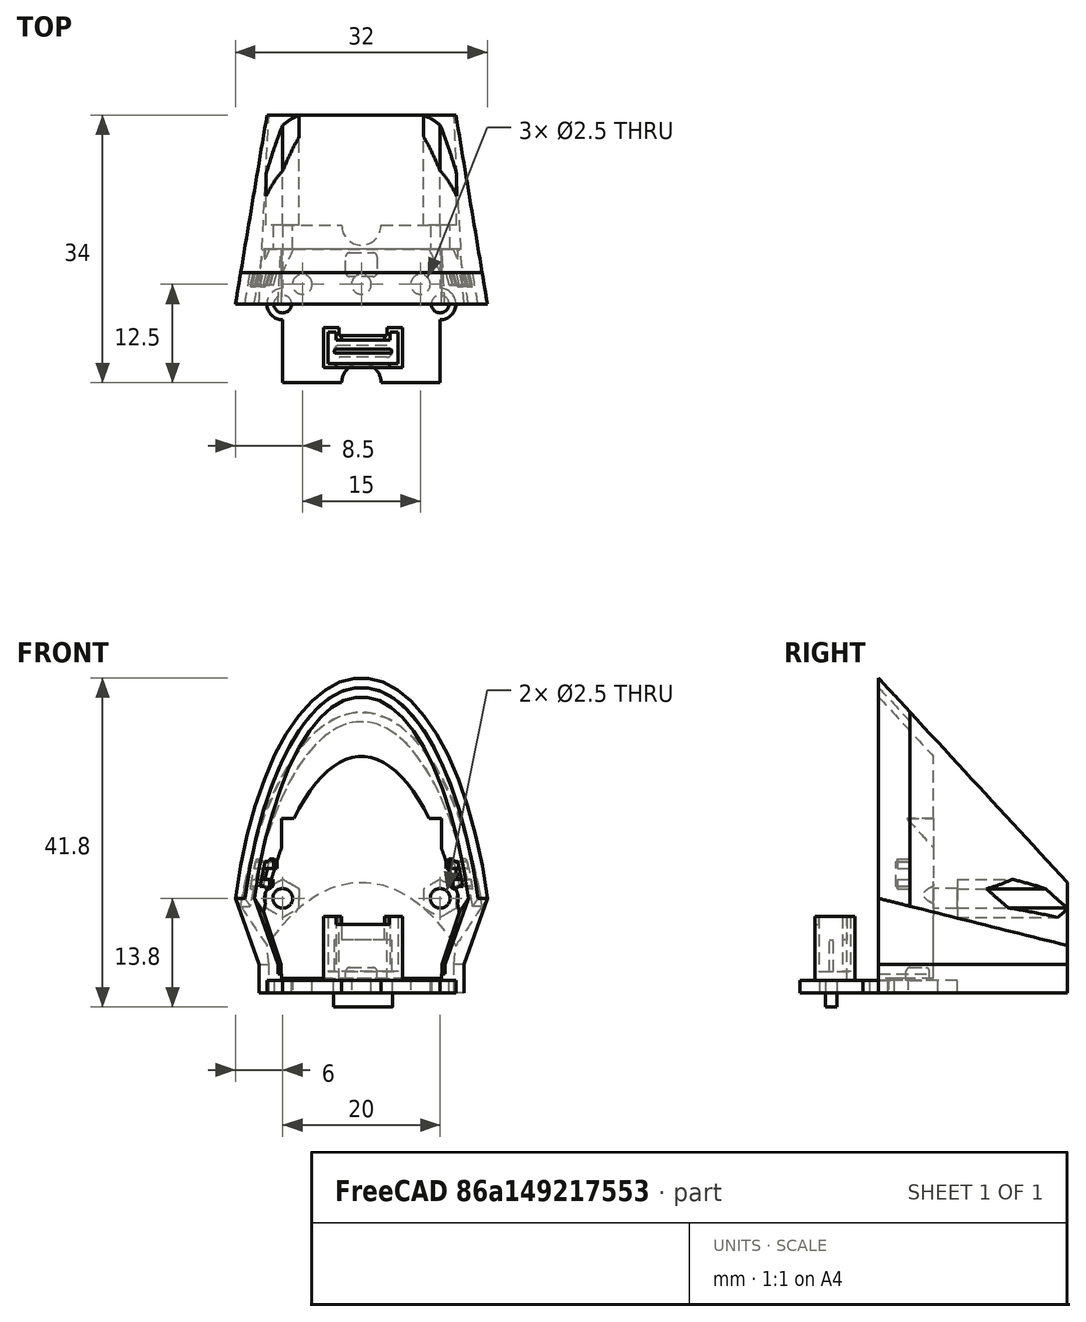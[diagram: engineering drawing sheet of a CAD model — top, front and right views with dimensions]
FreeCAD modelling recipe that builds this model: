
FCSTD DOCUMENT  (FreeCAD 0.19R24276 (Git))
Label: Phoebe_Ear
License: All rights reserved
LicenseURL: http://en.wikipedia.org/wiki/All_rights_reserved
objects: Sketcher::SketchObject×30, PartDesign::Pocket×9, PartDesign::Pad×7, PartDesign::Plane×5, PartDesign::Body×5, PartDesign::SubtractiveLoft×4, PartDesign::AdditiveLoft×2, App::Part×2, Mesh::Feature×2, Spreadsheet::Sheet×1, PartDesign::Fillet×1
note: 86 computed .brp shape members not serialized (recipe doc carries the construction recipe); baked Part::Feature solids carry a one-line shape summary decoded from their .brp

FEATURE [PartDesign::Plane] DatumPlane  label="Datum_EarBack"
  AttachmentOffset = pos=(0,0,-24) rot=(0,0,1;0rad)
  Length = 61.2949
  MapMode = 5
  Placement = pos=(0,24,5.3e-15) rot=(1,0,0;1.5708rad)
  ResizeMode = 0
  Support = -> [XZ_Plane001]
  Width = 75.0828
  expr: .AttachmentOffset.Base.z = -<<params>>.ear_leng
FEATURE [Spreadsheet::Sheet] Spreadsheet  label="params"
  cells = A1=M2 Bolt Clearances; C1=M2.5 Bolt Clearances; E1=Std Dims; G1=Grove Board Dims; A2=Hole Clear Diam; B2(m2_hole_clear_diam)==2.5mm; C2=Hole Clear Diam; D2(m25_hole_clear_diam)==2.8mm; E2=Std. Chamfer; F2(std_chamf)==1mm; G2=Grove Board Width; H2(grove_board_width)==20mm; A3=Head Clear Diam; B3(m2_head_clear_diam)==4.2mm; C3=Head Clear Diam; D3(m25_head_clear_diam)==5.3mm; E3=Std. Radius; F3(std_rad)==2mm; G3=Grove Board Outer Mt Diam; H3(grove_board_mt_outer_diam)==4mm; A4=Head Min Depth; B4(m2_head_min_depth)==1.6mm; C4=Head Min Depth; D4(m25_head_min_depth)==2.3mm; E4=Std. Clear Tol; F4(std_clear_tol)==0.3mm; A5=Nut Clear Flat; B5(m2_nut_clear_flat)==4.2mm; C5=Nut Clear Flat; D5(m25_nut_clear_flat)==5.2mm; A6=Nut Min Depth; B6(m2_nut_min_depth)==1.75mm; C6=Nut Min Depth; D6(m25_nut_min_depth)==2mm; A8=Ear Dims; A9=Ear Base Thick; B9(ear_base_thick)==2mm; C9=Ear Leng; D9(ear_leng)==24mm; E9=Mic Mt Plane Offset Z; F9(mic_mt_plane_offset_z)==7mm; A10=Ear Vert Height; B10(ear_vert_height)==1.6mm; C10=Ear Ellipse Maj Ax; D10(ear_ellipse_majax)==40mm; E10=Mic Mt Hex Offset; F10(mic_mt_hex_offset)==3mm; A12=Ear Fr Base Width; B12(ear_front_base_width)==26mm; C12=Ear Mt Hole Offset; D12(ear_mt_hole_offset)==2.5mm; A13=Ear Fr Mid Width; B13(ear_front_mid_width)==32mm; C13=Ear Mt Hole Width Space; D13(ear_mt_hole_width)==15mm; A14=Ear Fr Mid Height; B14(ear_front_mid_height)==12mm; A15=Ear Fr Tot Height; B15(ear_front_tot_height)==40mm; C15=Ear Wall Thick; D15(ear_wall_thick)==2.4mm; G15=Ear Trm Leng; H15(ear_trim_leng)==4mm; G16=Ear Trm Thick; H16(ear_trim_thick)==1.2mm; A17=Ear Bk Base Width; B17(ear_back_base_width)==23.5mm; C17=Ear Sl Base Width; D17(ear_slope_base_width)==(ear_front_base_width - ear_back_base_width) / ear_leng; E17=Ear GM Base Width; F17(ear_gm_base_width)==ear_front_base_width - ear_slope_base_width * mic_mt_plane_offset_z; G17=Ear Trm Base Width; H17(ear_trim_base_width)==ear_front_base_width - ear_slope_base_width * ear_trim_leng; A18=Ear Bk Mid Width; B18(ear_back_mid_width)==24mm; C18=Ear Sl Mid Width; D18(ear_slope_mid_width)==(ear_front_mid_width - ear_back_mid_width) / ear_leng; E18=Ear GM Mid Width; F18(ear_gm_mid_width)==ear_front_mid_width - ear_slope_mid_width * mic_mt_plane_offset_z; G18=Ear Trm Mid Width; H18(ear_trim_mid_width)==ear_front_mid_width - ear_slope_mid_width * ear_trim_leng; A19=Ear Bk Mid Height; B19(ear_back_mid_height)==6mm; C19=Ear Sl Mid Height; D19(ear_slope_mid_height)==(ear_front_mid_height - ear_back_mid_height) / ear_leng; E19=Ear GM Mid Height; F19(ear_gm_mid_height)==ear_front_mid_height - ear_slope_mid_height * mic_mt_plane_offset_z; G19=Ear Trm Mid Height; H19(ear_trim_mid_height)==ear_front_mid_height - ear_slope_mid_height * ear_trim_leng; A20=Ear Bk Tot Height; B20(ear_back_tot_height)==14mm; C20=Ear Sl Tot Height; D20(ear_slope_tot_height)==(ear_front_tot_height - ear_back_tot_height) / ear_leng; E20=Ear GM Tot Height; F20(ear_gm_tot_height)==ear_front_tot_height - ear_slope_tot_height * mic_mt_plane_offset_z; G20=Ear Trm Tot Height; H20(ear_trim_tot_height)==ear_front_tot_height - ear_slope_tot_height * ear_trim_leng; G22=Ear Trm Clip Width; H22(ear_trim_clip_width)==1.6mm; G23=Ear Trm Clip Height; H23(ear_trim_clip_height)==3mm; G24=Ear Trm Clip Tol; H24(ear_trim_clip_tol)==0.2mm; G25=Ear Trm Clip Thick; H25(ear_trim_clip_thick)==0.8mm; G26=Ear Trm Clip Wedge Size; H26(ear_trim_clip_wedge_size)==0.4mm; G27=Ear Trm Clip Leng; H27(ear_trim_clip_leng)==ear_wall_thick - ear_trim_thick + ear_trim_clip_tol
FEATURE [Sketcher::SketchObject] Sketch  label="Sketch_EarFront"
  FullyConstrained = true
  MapMode = 5
  Placement = pos=(0,0,0) rot=(1,0,0;1.5708rad)
  Support = -> [XZ_Plane001]
  expr: Constraints[30] = <<params>>.ear_base_thick + <<params>>.ear_vert_height
  expr: Constraints[31] = <<params>>.ear_front_mid_height
  expr: Constraints[32] = <<params>>.ear_front_mid_width
  expr: Constraints[33] = <<params>>.ear_front_base_width
  expr: Constraints[34] = <<params>>.ear_front_tot_height
  expr: Constraints[35] = <<params>>.ear_ellipse_majax
  sketch-geometry (15):
    g0: LineSegment StartX=-13 StartY=0 StartZ=0 EndX=13 EndY=0 EndZ=0
    g1: LineSegment StartX=-13 StartY=0 StartZ=0 EndX=-13 EndY=3.6 EndZ=0
    g2: LineSegment StartX=13 StartY=0 StartZ=0 EndX=13 EndY=3.6 EndZ=0
    g3: LineSegment StartX=-13 StartY=3.6 StartZ=0 EndX=13 EndY=3.6 EndZ=0
    g4: LineSegment StartX=13 StartY=3.6 StartZ=0 EndX=16 EndY=12 EndZ=0
    g5: LineSegment StartX=-13 StartY=3.6 StartZ=0 EndX=-16 EndY=12 EndZ=0
    g6: ArcOfEllipse CenterX=0 CenterY=4e-16 CenterZ=0 NormalX=0 NormalY=0 NormalZ=1 MajorRadius=40 MinorRadius=16.7726 AngleXU=1.5708 StartAngle=5.01708 EndAngle=7.54929
    g7: LineSegment StartX=0 StartY=40 StartZ=0 EndX=0 EndY=-40 EndZ=0
    g8: LineSegment StartX=-16.7726 StartY=4e-16 StartZ=0 EndX=16.7726 EndY=4e-16 EndZ=0
    g9: GeomPoint X=0 Y=36.3137 Z=0
    g10: GeomPoint X=0 Y=-36.3137 Z=0
    g11: LineSegment StartX=-16 StartY=12 StartZ=0 EndX=16 EndY=12 EndZ=0
    g12: LineSegment StartX=-13 StartY=3.6 StartZ=0 EndX=-13 EndY=12 EndZ=0
    g13: LineSegment StartX=13 StartY=3.6 StartZ=0 EndX=13 EndY=12 EndZ=0
    g14: LineSegment StartX=-16 StartY=12 StartZ=0 EndX=16 EndY=12 EndZ=0
  constraints (33):
    c: Horizontal(g0)
    c: Symmetric(g0,g0,g-1)
    c: Coincident(g1,g0)
    c: Vertical(g1)
    c: Coincident(g2,g0)
    c: Vertical(g2)
    c: Coincident(g3,g1)
    c: Coincident(g3,g2)
    c: Horizontal(g3)
    c: Coincident(g4,g2)
    c: Coincident(g5,g1)
    c: InternalAlignment(g7-g10 -> g6) x4
    c: PointOnObject(g6,g-2)
    c: Coincident(g11,g5)
    c: Coincident(g11,g4)
    c: Horizontal(g11)
    c: Coincident(g12,g1)
    c: PointOnObject(g12,g11)
    c: Vertical(g12)
    c: Coincident(g13,g2)
    c: PointOnObject(g13,g11)
    c: Vertical(g13)
    c: PointOnObject(g7,g-2)
    c: Coincident(g14,g6)
    c: Coincident(g14,g6)
    c: Coincident(g6,g5)
    c: Coincident(g6,g4)
    c: DistanceY(g0,g2) = 3.6
    c: DistanceY(g-1,g4) = 12
    c: DistanceX(g5,g4) = 32
    c: DistanceX(g0,g0) = 26
    c: DistanceY(g-1,g7) = 40
    c: DistanceY(g8,g7) = 40
FEATURE [Sketcher::SketchObject] Sketch001  label="Sketch_EarBack"
  FullyConstrained = true
  MapMode = 5
  Placement = pos=(0,24,5.3e-15) rot=(1,0,0;1.5708rad)
  Support = -> [DatumPlane]
  expr: Constraints[33] = <<params>>.ear_back_base_width
  expr: Constraints[32] = <<params>>.ear_back_mid_width
  expr: Constraints[31] = <<params>>.ear_back_mid_height
  expr: Constraints[30] = <<params>>.ear_base_thick + <<params>>.ear_vert_height
  expr: Constraints[34] = <<params>>.ear_back_tot_height
  expr: Constraints[35] = <<params>>.ear_ellipse_majax
  sketch-geometry (15):
    g0: LineSegment StartX=-11.75 StartY=0 StartZ=0 EndX=11.75 EndY=0 EndZ=0
    g1: LineSegment StartX=-11.75 StartY=0 StartZ=0 EndX=-11.75 EndY=3.6 EndZ=0
    g2: LineSegment StartX=11.75 StartY=0 StartZ=0 EndX=11.75 EndY=3.6 EndZ=0
    g3: LineSegment StartX=-11.75 StartY=3.6 StartZ=0 EndX=11.75 EndY=3.6 EndZ=0
    g4: LineSegment StartX=11.75 StartY=3.6 StartZ=0 EndX=12 EndY=6 EndZ=0
    g5: LineSegment StartX=-11.75 StartY=3.6 StartZ=0 EndX=-12 EndY=6 EndZ=0
    g6: ArcOfEllipse CenterX=0 CenterY=-26 CenterZ=0 NormalX=0 NormalY=0 NormalZ=1 MajorRadius=40 MinorRadius=20 AngleXU=1.5708 StartAngle=5.63968 EndAngle=6.92669
    g7: LineSegment StartX=0 StartY=14 StartZ=0 EndX=0 EndY=-66 EndZ=0
    g8: LineSegment StartX=-20 StartY=-26 StartZ=0 EndX=20 EndY=-26 EndZ=0
    g9: GeomPoint X=0 Y=8.64102 Z=0
    g10: GeomPoint X=0 Y=-60.641 Z=0
    g11: LineSegment StartX=-12 StartY=6 StartZ=0 EndX=12 EndY=6 EndZ=0
    g12: LineSegment StartX=-11.75 StartY=3.6 StartZ=0 EndX=-11.75 EndY=6 EndZ=0
    g13: LineSegment StartX=11.75 StartY=3.6 StartZ=0 EndX=11.75 EndY=6 EndZ=0
    g14: LineSegment StartX=-12 StartY=6 StartZ=0 EndX=12 EndY=6 EndZ=0
  constraints (33):
    c: Horizontal(g0)
    c: Symmetric(g0,g0,g-1)
    c: Coincident(g1,g0)
    c: Vertical(g1)
    c: Coincident(g2,g0)
    c: Vertical(g2)
    c: Coincident(g3,g1)
    c: Coincident(g3,g2)
    c: Horizontal(g3)
    c: Coincident(g4,g2)
    c: Coincident(g5,g1)
    c: InternalAlignment(g7-g10 -> g6) x4
    c: PointOnObject(g6,g-2)
    c: Coincident(g11,g5)
    c: Coincident(g11,g4)
    c: Horizontal(g11)
    c: Coincident(g12,g1)
    c: PointOnObject(g12,g11)
    c: Vertical(g12)
    c: Coincident(g13,g2)
    c: PointOnObject(g13,g11)
    c: Vertical(g13)
    c: PointOnObject(g7,g-2)
    c: Coincident(g14,g6)
    c: Coincident(g14,g6)
    c: Coincident(g6,g5)
    c: Coincident(g6,g4)
    c: DistanceY(g0,g2) = 3.6
    c: DistanceY(g-1,g4) = 6
    c: DistanceX(g5,g4) = 24
    c: DistanceX(g0,g0) = 23.5
    c: DistanceY(g-1,g7) = 14
    c: DistanceY(g6,g7) = 40
FEATURE [PartDesign::AdditiveLoft] AdditiveLoft  label="AdditiveLoft_MainEar"
  Closed = false
  Placement = pos=(0,0,0) rot=(1,0,0;1.5708rad)
  Profile = -> Sketch
  Ruled = false
  Sections = -> [Sketch001]
FEATURE [Sketcher::SketchObject] Sketch002
  FullyConstrained = true
  MapMode = 5
  Support = -> [XY_Plane001]
  expr: Constraints[7] = <<params>>.ear_mt_hole_width
  expr: Constraints[8] = <<params>>.ear_mt_hole_offset
  expr: Constraints[9] = <<params>>.m2_hole_clear_diam
  sketch-geometry (5):
    g0: LineSegment StartX=-7.5 StartY=2.5 StartZ=0 EndX=7.5 EndY=2.5 EndZ=0
    g1: GeomPoint X=0 Y=2.5 Z=0
    g2: Circle CenterX=0 CenterY=2.5 CenterZ=0 NormalX=0 NormalY=0 NormalZ=1 AngleXU=0 Radius=1.25
    g3: Circle CenterX=7.5 CenterY=2.5 CenterZ=0 NormalX=0 NormalY=0 NormalZ=1 AngleXU=0 Radius=1.25
    g4: Circle CenterX=-7.5 CenterY=2.5 CenterZ=0 NormalX=0 NormalY=0 NormalZ=1 AngleXU=0 Radius=1.25
  constraints (11):
    c: Horizontal(g0)
    c: PointOnObject(g1,g-2)
    c: Symmetric(g0,g0,g1)
    c: Coincident(g2,g1)
    c: Coincident(g3,g0)
    c: Coincident(g4,g0)
    c: Equal(g2,g3)
    c: DistanceX(g4,g3) = 15
    c: DistanceY(g-1,g2) = 2.5
    c: Diameter(g3) = 2.5
    c: Equal(g2,g4)
FEATURE [PartDesign::Pocket] Pocket  label="Pocket_MtHoles"
  BaseFeature = -> AdditiveLoft
  Length = 6
  Length2 = 100
  Placement = pos=(0,0,0) rot=(1,0,0;1.5708rad)
  Profile = -> Sketch002
  Reversed = true
  Type = 0
  expr: Length = <<params>>.ear_base_thick * 3
FEATURE [Sketcher::SketchObject] Sketch003  label="Sketch_EarFr_Temp"
  FullyConstrained = true
  MapMode = 5
  Placement = pos=(0,0,0) rot=(1,0,0;1.5708rad)
  Support = -> [XZ_Plane001]
  expr: Constraints[35] = <<params>>.ear_ellipse_majax
  expr: Constraints[34] = <<params>>.ear_front_tot_height
  expr: Constraints[33] = <<params>>.ear_front_base_width
  expr: Constraints[32] = <<params>>.ear_front_mid_width
  expr: Constraints[31] = <<params>>.ear_front_mid_height
  expr: Constraints[30] = <<params>>.ear_base_thick + <<params>>.ear_vert_height
  sketch-geometry (15):
    g0: LineSegment StartX=-13 StartY=0 StartZ=0 EndX=13 EndY=0 EndZ=0
    g1: LineSegment StartX=-13 StartY=0 StartZ=0 EndX=-13 EndY=3.6 EndZ=0
    g2: LineSegment StartX=13 StartY=0 StartZ=0 EndX=13 EndY=3.6 EndZ=0
    g3: LineSegment StartX=-13 StartY=3.6 StartZ=0 EndX=13 EndY=3.6 EndZ=0
    g4: LineSegment StartX=13 StartY=3.6 StartZ=0 EndX=16 EndY=12 EndZ=0
    g5: LineSegment StartX=-13 StartY=3.6 StartZ=0 EndX=-16 EndY=12 EndZ=0
    g6: ArcOfEllipse CenterX=0 CenterY=-7e-16 CenterZ=0 NormalX=0 NormalY=0 NormalZ=1 MajorRadius=40 MinorRadius=16.7726 AngleXU=1.5708 StartAngle=5.01708 EndAngle=7.54929
    g7: LineSegment StartX=0 StartY=40 StartZ=0 EndX=0 EndY=-40 EndZ=0
    g8: LineSegment StartX=-16.7726 StartY=-7e-16 StartZ=0 EndX=16.7726 EndY=-7e-16 EndZ=0
    g9: GeomPoint X=0 Y=36.3137 Z=0
    g10: GeomPoint X=0 Y=-36.3137 Z=0
    g11: LineSegment StartX=-16 StartY=12 StartZ=0 EndX=16 EndY=12 EndZ=0
    g12: LineSegment StartX=-13 StartY=3.6 StartZ=0 EndX=-13 EndY=12 EndZ=0
    g13: LineSegment StartX=13 StartY=3.6 StartZ=0 EndX=13 EndY=12 EndZ=0
    g14: LineSegment StartX=-16 StartY=12 StartZ=0 EndX=16 EndY=12 EndZ=0
  constraints (33):
    c: Horizontal(g0)
    c: Symmetric(g0,g0,g-1)
    c: Coincident(g1,g0)
    c: Vertical(g1)
    c: Coincident(g2,g0)
    c: Vertical(g2)
    c: Coincident(g3,g1)
    c: Coincident(g3,g2)
    c: Horizontal(g3)
    c: Coincident(g4,g2)
    c: Coincident(g5,g1)
    c: InternalAlignment(g7-g10 -> g6) x4
    c: PointOnObject(g6,g-2)
    c: Coincident(g11,g5)
    c: Coincident(g11,g4)
    c: Horizontal(g11)
    c: Coincident(g12,g1)
    c: PointOnObject(g12,g11)
    c: Vertical(g12)
    c: Coincident(g13,g2)
    c: PointOnObject(g13,g11)
    c: Vertical(g13)
    c: PointOnObject(g7,g-2)
    c: Coincident(g14,g6)
    c: Coincident(g14,g6)
    c: Coincident(g6,g5)
    c: Coincident(g6,g4)
    c: DistanceY(g0,g2) = 3.6
    c: DistanceY(g-1,g4) = 12
    c: DistanceX(g5,g4) = 32
    c: DistanceX(g0,g0) = 26
    c: DistanceY(g-1,g7) = 40
    c: DistanceY(g8,g7) = 40
FEATURE [Sketcher::SketchObject] Sketch004  label="Sketch_EarBk_Temp"
  FullyConstrained = true
  MapMode = 5
  Placement = pos=(0,24,5.3e-15) rot=(1,0,0;1.5708rad)
  Support = -> [DatumPlane]
  expr: Constraints[35] = <<params>>.ear_ellipse_majax
  expr: Constraints[34] = <<params>>.ear_back_tot_height
  expr: Constraints[30] = <<params>>.ear_base_thick + <<params>>.ear_vert_height
  expr: Constraints[31] = <<params>>.ear_back_mid_height
  expr: Constraints[32] = <<params>>.ear_back_mid_width
  expr: Constraints[33] = <<params>>.ear_back_base_width
  sketch-geometry (15):
    g0: LineSegment StartX=-11.75 StartY=0 StartZ=0 EndX=11.75 EndY=0 EndZ=0
    g1: LineSegment StartX=-11.75 StartY=0 StartZ=0 EndX=-11.75 EndY=3.6 EndZ=0
    g2: LineSegment StartX=11.75 StartY=0 StartZ=0 EndX=11.75 EndY=3.6 EndZ=0
    g3: LineSegment StartX=-11.75 StartY=3.6 StartZ=0 EndX=11.75 EndY=3.6 EndZ=0
    g4: LineSegment StartX=11.75 StartY=3.6 StartZ=0 EndX=12 EndY=6 EndZ=0
    g5: LineSegment StartX=-11.75 StartY=3.6 StartZ=0 EndX=-12 EndY=6 EndZ=0
    g6: ArcOfEllipse CenterX=0 CenterY=-26 CenterZ=0 NormalX=0 NormalY=0 NormalZ=1 MajorRadius=40 MinorRadius=20 AngleXU=1.5708 StartAngle=5.63968 EndAngle=6.92669
    g7: LineSegment StartX=0 StartY=14 StartZ=0 EndX=0 EndY=-66 EndZ=0
    g8: LineSegment StartX=-20 StartY=-26 StartZ=0 EndX=20 EndY=-26 EndZ=0
    g9: GeomPoint X=0 Y=8.64102 Z=0
    g10: GeomPoint X=0 Y=-60.641 Z=0
    g11: LineSegment StartX=-12 StartY=6 StartZ=0 EndX=12 EndY=6 EndZ=0
    g12: LineSegment StartX=-11.75 StartY=3.6 StartZ=0 EndX=-11.75 EndY=6 EndZ=0
    g13: LineSegment StartX=11.75 StartY=3.6 StartZ=0 EndX=11.75 EndY=6 EndZ=0
    g14: LineSegment StartX=-12 StartY=6 StartZ=0 EndX=12 EndY=6 EndZ=0
  constraints (33):
    c: Horizontal(g0)
    c: Symmetric(g0,g0,g-1)
    c: Coincident(g1,g0)
    c: Vertical(g1)
    c: Coincident(g2,g0)
    c: Vertical(g2)
    c: Coincident(g3,g1)
    c: Coincident(g3,g2)
    c: Horizontal(g3)
    c: Coincident(g4,g2)
    c: Coincident(g5,g1)
    c: InternalAlignment(g7-g10 -> g6) x4
    c: PointOnObject(g6,g-2)
    c: Coincident(g11,g5)
    c: Coincident(g11,g4)
    c: Horizontal(g11)
    c: Coincident(g12,g1)
    c: PointOnObject(g12,g11)
    c: Vertical(g12)
    c: Coincident(g13,g2)
    c: PointOnObject(g13,g11)
    c: Vertical(g13)
    c: PointOnObject(g7,g-2)
    c: Coincident(g14,g6)
    c: Coincident(g14,g6)
    c: Coincident(g6,g5)
    c: Coincident(g6,g4)
    c: DistanceY(g0,g2) = 3.6
    c: DistanceY(g-1,g4) = 6
    c: DistanceX(g5,g4) = 24
    c: DistanceX(g0,g0) = 23.5
    c: DistanceY(g-1,g7) = 14
    c: DistanceY(g6,g7) = 40
FEATURE [Sketcher::SketchObject] Sketch005
  FullyConstrained = true
  MapMode = 5
  Support = -> [XY_Plane003]
  sketch-geometry (16):
    g0: LineSegment StartX=-10 StartY=10 StartZ=0 EndX=-2.5 EndY=10 EndZ=0
    g1: LineSegment StartX=2.5 StartY=10 StartZ=0 EndX=10 EndY=10 EndZ=0
    g2: LineSegment StartX=10 StartY=10 StartZ=0 EndX=10 EndY=2 EndZ=0
    g3: LineSegment StartX=10 StartY=-2 StartZ=0 EndX=10 EndY=-10 EndZ=0
    g4: LineSegment StartX=10 StartY=-10 StartZ=0 EndX=2.5 EndY=-10 EndZ=0
    g5: LineSegment StartX=-2.5 StartY=-10 StartZ=0 EndX=-10 EndY=-10 EndZ=0
    g6: LineSegment StartX=-10 StartY=-10 StartZ=0 EndX=-10 EndY=-2 EndZ=0
    g7: LineSegment StartX=-10 StartY=10 StartZ=0 EndX=-10 EndY=2 EndZ=0
    g8: ArcOfCircle CenterX=0 CenterY=10 CenterZ=0 NormalX=0 NormalY=0 NormalZ=1 AngleXU=0 Radius=2.5 StartAngle=3.14159 EndAngle=6.28319
    g9: ArcOfCircle CenterX=0 CenterY=-10 CenterZ=0 NormalX=0 NormalY=0 NormalZ=1 AngleXU=0 Radius=2.5 StartAngle=0 EndAngle=3.14159
    g10: LineSegment StartX=-2.5 StartY=10 StartZ=0 EndX=2.5 EndY=10 EndZ=0
    g11: LineSegment StartX=-2.5 StartY=-10 StartZ=0 EndX=2.5 EndY=-10 EndZ=0
    g12: LineSegment StartX=-10 StartY=2 StartZ=0 EndX=-10 EndY=-2 EndZ=0
    g13: LineSegment StartX=10 StartY=2 StartZ=0 EndX=10 EndY=-2 EndZ=0
    g14: ArcOfCircle CenterX=-10 CenterY=0 CenterZ=0 NormalX=0 NormalY=0 NormalZ=1 AngleXU=0 Radius=2 StartAngle=1.5708 EndAngle=4.71239
    g15: ArcOfCircle CenterX=10 CenterY=0 CenterZ=0 NormalX=0 NormalY=0 NormalZ=1 AngleXU=0 Radius=2 StartAngle=4.71239 EndAngle=7.85398
  constraints (48):
    c: Horizontal(g0)
    c: Horizontal(g1)
    c: Coincident(g2,g1)
    c: Vertical(g2)
    c: Vertical(g3)
    c: Coincident(g4,g3)
    c: Horizontal(g4)
    c: Horizontal(g5)
    c: Coincident(g6,g5)
    c: Vertical(g6)
    c: Coincident(g7,g0)
    c: Vertical(g7)
    c: PointOnObject(g8,g-2)
    c: Coincident(g8,g0)
    c: Coincident(g8,g1)
    c: PointOnObject(g9,g-2)
    c: Coincident(g9,g5)
    c: Coincident(g9,g4)
    c: Coincident(g10,g0)
    c: Coincident(g10,g1)
    c: Coincident(g11,g5)
    c: Coincident(g11,g4)
    c: Horizontal(g11)
    c: PointOnObject(g9,g11)
    c: PointOnObject(g8,g10)
    c: Horizontal(g10)
    c: Coincident(g12,g7)
    c: Coincident(g12,g6)
    c: Coincident(g13,g2)
    c: Coincident(g13,g3)
    c: Equal(g10,g11)
    c: Equal(g13,g12)
    c: Vertical(g12)
    c: Vertical(g13)
    c: PointOnObject(g14,g-1)
    c: Coincident(g14,g7)
    c: Coincident(g14,g6)
    c: PointOnObject(g15,g-1)
    c: Coincident(g15,g2)
    c: Coincident(g15,g3)
    c: PointOnObject(g14,g12)
    c: PointOnObject(g15,g13)
    c: Equal(g7,g6)
    c: Equal(g1,g0)
    c: Diameter(g14) = 4
    c: Diameter(g8) = 5
    c: DistanceY(g3,g1) = 20
    c: DistanceX(g0,g1) = 20
FEATURE [PartDesign::Pad] Pad
  Direction = (1,1,1)
  Length = 1.6
  Length2 = 100
  Profile = -> Sketch005
  Type = 0
FEATURE [Sketcher::SketchObject] Sketch006
  FullyConstrained = true
  MapMode = 5
  Support = -> [XY_Plane003]
  sketch-geometry (2):
    g0: Circle CenterX=-10 CenterY=0 CenterZ=0 NormalX=0 NormalY=0 NormalZ=1 AngleXU=0 Radius=1.125
    g1: Circle CenterX=10 CenterY=0 CenterZ=0 NormalX=0 NormalY=0 NormalZ=1 AngleXU=0 Radius=1.125
  constraints (5):
    c: PointOnObject(g1,g-1)
    c: Symmetric(g0,g1,g-1)
    c: Equal(g0,g1)
    c: Diameter(g0) = 2.25
    c: DistanceX(g0,g1) = 20
FEATURE [PartDesign::Pocket] Pocket006
  BaseFeature = -> Pad
  Length = 5
  Length2 = 100
  Profile = -> Sketch006
  Reversed = true
  Type = 1
FEATURE [PartDesign::Body] Body007  label="GroveBoard"
  Group = -> [Sketch005,Pad,Sketch006,Pocket006]
  Origin = -> Origin002
  Tip = -> Pocket006
FEATURE [Sketcher::SketchObject] Sketch008
  FullyConstrained = true
  MapMode = 5
  Support = -> [XY_Plane007]
  sketch-geometry (8):
    g0: LineSegment StartX=-5 StartY=0 StartZ=0 EndX=-3.05 EndY=0 EndZ=0
    g1: LineSegment StartX=3.05 StartY=0 StartZ=0 EndX=5 EndY=0 EndZ=0
    g2: LineSegment StartX=-5 StartY=0 StartZ=0 EndX=-5 EndY=5.1 EndZ=0
    g3: LineSegment StartX=-5 StartY=5.1 StartZ=0 EndX=5 EndY=5.1 EndZ=0
    g4: LineSegment StartX=5 StartY=5.1 StartZ=0 EndX=5 EndY=0 EndZ=0
    g5: LineSegment StartX=3.05 StartY=0 StartZ=0 EndX=3.05 EndY=1 EndZ=0
    g6: LineSegment StartX=3.05 StartY=1 StartZ=0 EndX=-3.05 EndY=1 EndZ=0
    g7: LineSegment StartX=-3.05 StartY=1 StartZ=0 EndX=-3.05 EndY=0 EndZ=0
  constraints (23):
    c: PointOnObject(g0,g-1)
    c: PointOnObject(g1,g-1)
    c: PointOnObject(g0,g-1)
    c: Coincident(g2,g0)
    c: Vertical(g2)
    c: Coincident(g3,g2)
    c: Horizontal(g3)
    c: Coincident(g4,g3)
    c: Coincident(g4,g1)
    c: Vertical(g4)
    c: Coincident(g5,g1)
    c: Vertical(g5)
    c: Coincident(g6,g5)
    c: Horizontal(g6)
    c: Coincident(g7,g6)
    c: Coincident(g7,g0)
    c: Vertical(g7)
    c: Equal(g0,g1)
    c: Symmetric(g0,g1,g-1)
    c: Distance(g4) = 5.1
    c: Distance(g6) = 6.1
    c: Distance(g3) = 10
    c: Distance(g7) = 1
FEATURE [PartDesign::Pad] Pad005
  Direction = (1,1,1)
  Length = 8.1
  Length2 = 100
  Profile = -> Sketch008
  Type = 0
FEATURE [Sketcher::SketchObject] Sketch009
  FullyConstrained = true
  MapMode = 5
  Placement = pos=(0,0,8.1) rot=(0,0,1;0rad)
  Support = -> [Pad005]
  sketch-geometry (10):
    g0: LineSegment StartX=-4.45 StartY=0.55 StartZ=0 EndX=-3.45 EndY=0.55 EndZ=0
    g1: LineSegment StartX=-3.45 StartY=0.55 StartZ=0 EndX=-3.45 EndY=1.55 EndZ=0
    g2: LineSegment StartX=-3.45 StartY=1.55 StartZ=0 EndX=3.45 EndY=1.55 EndZ=0
    g3: LineSegment StartX=3.45 StartY=1.55 StartZ=0 EndX=3.45 EndY=0.55 EndZ=0
    g4: LineSegment StartX=3.45 StartY=0.55 StartZ=0 EndX=4.45 EndY=0.55 EndZ=0
    g5: LineSegment StartX=4.45 StartY=0.55 StartZ=0 EndX=4.45 EndY=4.55 EndZ=0
    g6: LineSegment StartX=4.45 StartY=4.55 StartZ=0 EndX=-4.45 EndY=4.55 EndZ=0
    g7: LineSegment StartX=-4.45 StartY=4.55 StartZ=0 EndX=-4.45 EndY=0.55 EndZ=0
    g8: LineSegment StartX=-3.45 StartY=0.55 StartZ=0 EndX=3.45 EndY=0.55 EndZ=0
    g9: LineSegment StartX=0 StartY=0 StartZ=0 EndX=0 EndY=0.55 EndZ=0
  constraints (28):
    c: Horizontal(g0)
    c: Coincident(g1,g0)
    c: Coincident(g2,g1)
    c: Horizontal(g2)
    c: Coincident(g3,g2)
    c: Vertical(g3)
    c: Coincident(g4,g3)
    c: Horizontal(g4)
    c: Coincident(g5,g4)
    c: Vertical(g5)
    c: Coincident(g6,g5)
    c: Horizontal(g6)
    c: Coincident(g7,g6)
    c: Coincident(g7,g0)
    c: Vertical(g7)
    c: Vertical(g1)
    c: Coincident(g8,g0)
    c: Coincident(g8,g3)
    c: Horizontal(g8)
    c: Equal(g0,g4)
    c: Coincident(g9,g-1)
    c: PointOnObject(g9,g-2)
    c: Symmetric(g0,g3,g9)
    c: Distance(g0) = 1
    c: Distance(g1) = 1
    c: Distance(g9) = 0.55
    c: Distance(g6) = 8.9
    c: DistanceY(g2,g5) = 3
FEATURE [PartDesign::Pocket] Pocket003
  BaseFeature = -> Pad005
  Length = 7
  Length2 = 100
  Profile = -> Sketch009
  Type = 0
FEATURE [Sketcher::SketchObject] Sketch010
  FullyConstrained = true
  MapMode = 5
  Placement = pos=(0,0,8.1) rot=(0,0,1;0rad)
  Support = -> [Pocket003]
  sketch-geometry (5):
    g0: LineSegment StartX=0 StartY=0 StartZ=0 EndX=0 EndY=3 EndZ=0
    g1: LineSegment StartX=-3.4 StartY=8 StartZ=0 EndX=3.4 EndY=8 EndZ=0
    g2: LineSegment StartX=3.4 StartY=8 StartZ=0 EndX=3.4 EndY=3 EndZ=0
    g3: LineSegment StartX=3.4 StartY=3 StartZ=0 EndX=-3.4 EndY=3 EndZ=0
    g4: LineSegment StartX=-3.4 StartY=3 StartZ=0 EndX=-3.4 EndY=8 EndZ=0
  constraints (14):
    c: Coincident(g0,g-1)
    c: PointOnObject(g0,g-2)
    c: Coincident(g1,g2)
    c: Coincident(g2,g3)
    c: Coincident(g3,g4)
    c: Coincident(g4,g1)
    c: Horizontal(g1)
    c: Horizontal(g3)
    c: Vertical(g2)
    c: Vertical(g4)
    c: Symmetric(g3,g2,g0)
    c: Distance(g0) = 3
    c: Distance(g2) = 5
    c: Distance(g1) = 6.8
FEATURE [PartDesign::Pocket] Pocket004
  BaseFeature = -> Pocket003
  Length = 1
  Length2 = 100
  Profile = -> Sketch010
  Type = 0
FEATURE [Sketcher::SketchObject] Sketch011
  FullyConstrained = true
  MapMode = 5
  Placement = pos=(0,0,8.1) rot=(0,0,1;0rad)
  Support = -> [Pocket004]
  sketch-geometry (4):
    g0: LineSegment StartX=-2.75 StartY=3 StartZ=0 EndX=2.75 EndY=3 EndZ=0
    g1: LineSegment StartX=2.75 StartY=3 StartZ=0 EndX=2.75 EndY=0 EndZ=0
    g2: LineSegment StartX=2.75 StartY=0 StartZ=0 EndX=-2.75 EndY=0 EndZ=0
    g3: LineSegment StartX=-2.75 StartY=0 StartZ=0 EndX=-2.75 EndY=3 EndZ=0
  constraints (11):
    c: Coincident(g0,g1)
    c: Coincident(g1,g2)
    c: Coincident(g2,g3)
    c: Coincident(g3,g0)
    c: Horizontal(g0)
    c: Horizontal(g2)
    c: Vertical(g1)
    c: Vertical(g3)
    c: Symmetric(g2,g1,g-1)
    c: Distance(g1) = 3
    c: Distance(g0) = 5.5
FEATURE [PartDesign::Pocket] Pocket005
  BaseFeature = -> Pocket004
  Length = 3
  Length2 = 100
  Profile = -> Sketch011
  Type = 0
FEATURE [Sketcher::SketchObject] Sketch012
  FullyConstrained = true
  MapMode = 5
  Placement = pos=(0,0,1.1) rot=(0,0,1;0rad)
  Support = -> [Pocket005]
  sketch-geometry (5):
    g0: ArcOfCircle CenterX=-3.4 CenterY=3 CenterZ=0 NormalX=0 NormalY=0 NormalZ=1 AngleXU=0 Radius=0.25 StartAngle=1.5708 EndAngle=4.71239
    g1: ArcOfCircle CenterX=3.4 CenterY=3 CenterZ=0 NormalX=0 NormalY=0 NormalZ=1 AngleXU=0 Radius=0.25 StartAngle=4.71239 EndAngle=7.85398
    g2: LineSegment StartX=-3.4 StartY=2.75 StartZ=0 EndX=3.4 EndY=2.75 EndZ=0
    g3: LineSegment StartX=-3.4 StartY=3.25 StartZ=0 EndX=3.4 EndY=3.25 EndZ=0
    g4: LineSegment StartX=0 StartY=0 StartZ=0 EndX=0 EndY=2.75 EndZ=0
  constraints (12):
    c: Tangent(g0,g3) = 1.5708
    c: Tangent(g0,g2) = -1.5708
    c: Tangent(g2,g1) = -1.5708
    c: Tangent(g3,g1) = 1.5708
    c: Horizontal(g2)
    c: Equal(g0,g1)
    c: Coincident(g4,g-1)
    c: PointOnObject(g4,g-2)
    c: Symmetric(g0,g1,g4)
    c: DistanceY(g-1,g1) = 3
    c: DistanceY(g1,g1) = 0.5
    c: DistanceX(g0,g1) = 6.8
FEATURE [PartDesign::Pad] Pad006
  BaseFeature = -> Pocket005
  Direction = (1,1,1)
  Length = 4
  Length2 = 100
  Profile = -> Sketch012
  Type = 0
FEATURE [Sketcher::SketchObject] Sketch013
  FullyConstrained = true
  MapMode = 5
  Support = -> [XY_Plane007]
  sketch-geometry (5):
    g0: ArcOfCircle CenterX=-3 CenterY=3 CenterZ=0 NormalX=0 NormalY=0 NormalZ=1 AngleXU=0 Radius=0.75 StartAngle=1.5708 EndAngle=4.71239
    g1: ArcOfCircle CenterX=3 CenterY=3 CenterZ=0 NormalX=0 NormalY=0 NormalZ=1 AngleXU=0 Radius=0.75 StartAngle=4.71239 EndAngle=7.85398
    g2: LineSegment StartX=-3 StartY=2.25 StartZ=0 EndX=3 EndY=2.25 EndZ=0
    g3: LineSegment StartX=-3 StartY=3.75 StartZ=0 EndX=3 EndY=3.75 EndZ=0
    g4: LineSegment StartX=0 StartY=0 StartZ=0 EndX=0 EndY=3 EndZ=0
  constraints (12):
    c: Tangent(g0,g3) = 1.5708
    c: Tangent(g0,g2) = -1.5708
    c: Tangent(g2,g1) = -1.5708
    c: Tangent(g3,g1) = 1.5708
    c: Horizontal(g2)
    c: Equal(g0,g1)
    c: Coincident(g4,g-1)
    c: PointOnObject(g4,g-2)
    c: Symmetric(g0,g1,g4)
    c: Distance(g4) = 3
    c: DistanceY(g1,g1) = 1.5
    c: DistanceX(g0,g1) = 6
FEATURE [PartDesign::Pad] Pad007
  BaseFeature = -> Pad006
  Direction = (1,1,1)
  Length = 3.4
  Length2 = 100
  Profile = -> Sketch013
  Reversed = true
  Type = 0
FEATURE [PartDesign::Body] Body005  label="GroveHeader1"
  Group = -> [Sketch008,Pad005,Sketch009,Pocket003,Sketch010,Pocket004,Sketch011,Pocket005,Sketch012,Pad006,Sketch013,Pad007]
  Origin = -> Origin007
  Placement = pos=(0.2,-3,1.6) rot=(0,0,1;3.14159rad)
  Tip = -> Pad007
FEATURE [Sketcher::SketchObject] Sketch014
  FullyConstrained = true
  MapMode = 5
  Support = -> [XY_Plane008]
  sketch-geometry (8):
    g0: LineSegment StartX=-1.5 StartY=1.5 StartZ=0 EndX=1.5 EndY=1.5 EndZ=0
    g1: LineSegment StartX=2 StartY=1 StartZ=0 EndX=2 EndY=-1 EndZ=0
    g2: LineSegment StartX=1.5 StartY=-1.5 StartZ=0 EndX=-1.5 EndY=-1.5 EndZ=0
    g3: LineSegment StartX=-2 StartY=-1 StartZ=0 EndX=-2 EndY=1 EndZ=0
    g4: ArcOfCircle CenterX=-1.5 CenterY=1 CenterZ=0 NormalX=0 NormalY=0 NormalZ=1 AngleXU=0 Radius=0.5 StartAngle=1.5708 EndAngle=3.14159
    g5: ArcOfCircle CenterX=1.5 CenterY=1 CenterZ=0 NormalX=0 NormalY=0 NormalZ=1 AngleXU=0 Radius=0.5 StartAngle=0 EndAngle=1.5708
    g6: ArcOfCircle CenterX=1.5 CenterY=-1 CenterZ=0 NormalX=0 NormalY=0 NormalZ=1 AngleXU=0 Radius=0.5 StartAngle=4.71239 EndAngle=6.28319
    g7: ArcOfCircle CenterX=-1.5 CenterY=-1 CenterZ=0 NormalX=0 NormalY=0 NormalZ=1 AngleXU=0 Radius=0.5 StartAngle=3.14159 EndAngle=4.71239
  constraints (19):
    c: Horizontal(g0)
    c: Horizontal(g2)
    c: Vertical(g1)
    c: Vertical(g3)
    c: Tangent(g3,g4) = 1.5708
    c: Tangent(g0,g4) = 1.5708
    c: Tangent(g0,g5) = 1.5708
    c: Tangent(g1,g5) = 1.5708
    c: Tangent(g1,g6) = 1.5708
    c: Tangent(g2,g6) = 1.5708
    c: Tangent(g2,g7) = 1.5708
    c: Tangent(g3,g7) = 1.5708
    c: Equal(g4,g7)
    c: Equal(g5,g4)
    c: Equal(g5,g6)
    c: Symmetric(g5,g7,g-1)
    c: Radius(g5) = 0.5
    c: DistanceX(g3,g1) = 4
    c: DistanceY(g2,g0) = 3
FEATURE [PartDesign::Pad] Pad008
  Direction = (1,1,1)
  Length = 1.6
  Length2 = 100
  Profile = -> Sketch014
  Type = 0
FEATURE [PartDesign::Fillet] Fillet
  Base = -> Pad008 [Edge10]
  BaseFeature = -> Pad008
  Radius = 0.5
  SupportTransform = false
FEATURE [PartDesign::Body] Body006  label="MEMSMic"
  Group = -> [Sketch014,Pad008,Fillet]
  Origin = -> Origin008
  Placement = pos=(0,5,1.6) rot=(0,0,1;0rad)
  Tip = -> Fillet
FEATURE [App::Part] Part001  label="Grove_AnalogMic"
  Group = -> [Body007,Body005,Body006]
  Origin = -> Origin009
  Placement = pos=(0,7,12.1) rot=(-1,0,0;4.71239rad)
FEATURE [PartDesign::Plane] DatumPlane001  label="Datum_MicMtPlane"
  AttachmentOffset = pos=(0,0,-7) rot=(0,0,1;0rad)
  Length = 61.2949
  MapMode = 5
  Placement = pos=(0,7,1.6e-15) rot=(1,0,0;1.5708rad)
  ResizeMode = 0
  Support = -> [XZ_Plane001]
  Width = 75.0828
  expr: .AttachmentOffset.Base.z = -<<params>>.mic_mt_plane_offset_z
FEATURE [Sketcher::SketchObject] Sketch015  label="Sketch_GrovePCut"
  FullyConstrained = true
  MapMode = 5
  Placement = pos=(0,7,1.6e-15) rot=(1,0,0;1.5708rad)
  Support = -> [DatumPlane001]
  expr: Constraints[30] = <<params>>.grove_board_width + <<params>>.std_clear_tol
  expr: Constraints[32] = <<params>>.grove_board_mt_outer_diam + <<params>>.std_clear_tol
  expr: Constraints[29] = <<params>>.grove_board_width + <<params>>.std_clear_tol
  expr: Constraints[4] = <<params>>.ear_base_thick - <<params>>.std_clear_tol / 2
  sketch-geometry (12):
    g0: LineSegment StartX=-10.15 StartY=22.15 StartZ=0 EndX=10.15 EndY=22.15 EndZ=0
    g1: LineSegment StartX=10.15 StartY=1.85 StartZ=0 EndX=-10.15 EndY=1.85 EndZ=0
    g2: GeomPoint X=0 Y=1.85 Z=0
    g3: LineSegment StartX=-10.15 StartY=22.15 StartZ=0 EndX=-10.15 EndY=14.15 EndZ=0
    g4: LineSegment StartX=-10.15 StartY=1.85 StartZ=0 EndX=-10.15 EndY=9.85 EndZ=0
    g5: LineSegment StartX=10.15 StartY=1.85 StartZ=0 EndX=10.15 EndY=9.85 EndZ=0
    g6: LineSegment StartX=10.15 StartY=22.15 StartZ=0 EndX=10.15 EndY=14.15 EndZ=0
    g7: ArcOfCircle CenterX=-10.15 CenterY=12 CenterZ=0 NormalX=0 NormalY=0 NormalZ=1 AngleXU=0 Radius=2.15 StartAngle=1.5708 EndAngle=4.71239
    g8: ArcOfCircle CenterX=10.15 CenterY=12 CenterZ=0 NormalX=0 NormalY=0 NormalZ=1 AngleXU=0 Radius=2.15 StartAngle=4.71239 EndAngle=7.85398
    g9: LineSegment StartX=-10.15 StartY=14.15 StartZ=0 EndX=-10.15 EndY=9.85 EndZ=0
    g10: LineSegment StartX=10.15 StartY=14.15 StartZ=0 EndX=10.15 EndY=9.85 EndZ=0
    g11: LineSegment StartX=-10.15 StartY=12 StartZ=0 EndX=10.15 EndY=12 EndZ=0
  constraints (33):
    c: Horizontal(g0)
    c: Horizontal(g1)
    c: PointOnObject(g2,g-2)
    c: Symmetric(g1,g1,g2)
    c: DistanceY(g-1,g2) = 1.85
    c: Coincident(g3,g0)
    c: Vertical(g3)
    c: Coincident(g4,g1)
    c: Vertical(g4)
    c: Coincident(g5,g1)
    c: Vertical(g5)
    c: Coincident(g6,g0)
    c: Vertical(g6)
    c: Coincident(g7,g3)
    c: Coincident(g7,g4)
    c: Coincident(g8,g6)
    c: Coincident(g8,g5)
    c: Coincident(g9,g3)
    c: Coincident(g9,g4)
    c: Vertical(g9)
    c: Coincident(g10,g6)
    c: Coincident(g10,g5)
    c: Vertical(g10)
    c: PointOnObject(g7,g9)
    c: PointOnObject(g8,g10)
    c: Coincident(g11,g7)
    c: Coincident(g11,g8)
    c: Horizontal(g11)
    c: Equal(g6,g5)
    c: DistanceY(g1,g0) = 20.3
    c: DistanceX(g0,g0) = 20.3
    c: Equal(g8,g7)
    c: Diameter(g8) = 4.3
FEATURE [PartDesign::Pocket] Pocket007  label="Pocket_GroveMicMt"
  BaseFeature = -> Pocket
  Length = 5
  Length2 = 100
  Placement = pos=(0,0,0) rot=(1,0,0;1.5708rad)
  Profile = -> Sketch015
  Reversed = true
  Type = 1
FEATURE [Sketcher::SketchObject] Sketch016  label="Sketch_EarFront_Cut"
  FullyConstrained = true
  MapMode = 5
  Placement = pos=(0,0,0) rot=(1,0,0;1.5708rad)
  Support = -> [XZ_Plane001]
  expr: Constraints[61] = <<params>>.ear_ellipse_majax
  expr: Constraints[52] = <<params>>.ear_wall_thick
  expr: Constraints[60] = <<params>>.ear_wall_thick
  expr: Constraints[35] = <<params>>.ear_ellipse_majax
  expr: Constraints[50] = Spreadsheet.ear_wall_thick
  expr: Constraints[34] = <<params>>.ear_front_tot_height
  expr: Constraints[49] = Spreadsheet.ear_wall_thick
  expr: Constraints[33] = <<params>>.ear_front_base_width
  expr: Constraints[32] = <<params>>.ear_front_mid_width
  expr: Constraints[51] = <<params>>.ear_wall_thick
  expr: Constraints[31] = <<params>>.ear_front_mid_height
  expr: Constraints[30] = <<params>>.ear_base_thick + <<params>>.ear_vert_height
  sketch-geometry (26):
    g0: LineSegment StartX=-13 StartY=0 StartZ=0 EndX=13 EndY=0 EndZ=0
    g1: LineSegment StartX=-13 StartY=0 StartZ=0 EndX=-13 EndY=3.6 EndZ=0
    g2: LineSegment StartX=13 StartY=0 StartZ=0 EndX=13 EndY=3.6 EndZ=0
    g3: LineSegment StartX=-13 StartY=3.6 StartZ=0 EndX=13 EndY=3.6 EndZ=0
    g4: LineSegment StartX=13 StartY=3.6 StartZ=0 EndX=16 EndY=12 EndZ=0
    g5: LineSegment StartX=-13 StartY=3.6 StartZ=0 EndX=-16 EndY=12 EndZ=0
    g6: ArcOfEllipse CenterX=0 CenterY=7e-16 CenterZ=0 NormalX=0 NormalY=0 NormalZ=1 MajorRadius=40 MinorRadius=16.7726 AngleXU=1.5708 StartAngle=5.01708 EndAngle=7.54929
    g7: LineSegment StartX=0 StartY=40 StartZ=0 EndX=0 EndY=-40 EndZ=0
    g8: LineSegment StartX=-16.7726 StartY=7e-16 StartZ=0 EndX=16.7726 EndY=7e-16 EndZ=0
    g9: GeomPoint X=0 Y=36.3137 Z=0
    g10: GeomPoint X=0 Y=-36.3137 Z=0
    g11: LineSegment StartX=-16 StartY=12 StartZ=0 EndX=16 EndY=12 EndZ=0
    g12: LineSegment StartX=-13 StartY=3.6 StartZ=0 EndX=-13 EndY=12 EndZ=0
    g13: LineSegment StartX=13 StartY=3.6 StartZ=0 EndX=13 EndY=12 EndZ=0
    g14: LineSegment StartX=-16 StartY=12 StartZ=0 EndX=16 EndY=12 EndZ=0
    g15: LineSegment StartX=-10.6 StartY=2.4 StartZ=0 EndX=10.6 EndY=2.4 EndZ=0
    g16: GeomPoint X=0 Y=2.4 Z=0
    g17: LineSegment StartX=-10.6 StartY=2.4 StartZ=0 EndX=-10.6 EndY=3.6 EndZ=0
    g18: LineSegment StartX=-10.6 StartY=3.6 StartZ=0 EndX=-13.6 EndY=12 EndZ=0
    g19: LineSegment StartX=10.6 StartY=2.4 StartZ=0 EndX=10.6 EndY=3.6 EndZ=0
    g20: LineSegment StartX=10.6 StartY=3.6 StartZ=0 EndX=13.6 EndY=12 EndZ=0
    g21: ArcOfEllipse CenterX=0 CenterY=-2.4 CenterZ=0 NormalX=0 NormalY=0 NormalZ=1 MajorRadius=40 MinorRadius=14.5774 AngleXU=1.5708 StartAngle=5.08066 EndAngle=7.48571
    g22: LineSegment StartX=-7e-16 StartY=37.6 StartZ=0 EndX=7e-16 EndY=-42.4 EndZ=0
    g23: LineSegment StartX=-14.5774 StartY=-2.4 StartZ=0 EndX=14.5774 EndY=-2.4 EndZ=0
    g24: GeomPoint X=-6e-16 Y=34.8492 Z=0
    g25: GeomPoint X=6e-16 Y=-39.6492 Z=0
  constraints (56):
    c: Horizontal(g0)
    c: Symmetric(g0,g0,g-1)
    c: Coincident(g1,g0)
    c: Vertical(g1)
    c: Coincident(g2,g0)
    c: Vertical(g2)
    c: Coincident(g3,g1)
    c: Coincident(g3,g2)
    c: Horizontal(g3)
    c: Coincident(g4,g2)
    c: Coincident(g5,g1)
    c: InternalAlignment(g7-g10 -> g6) x4
    c: PointOnObject(g6,g-2)
    c: Coincident(g11,g5)
    c: Coincident(g11,g4)
    c: Horizontal(g11)
    c: Coincident(g12,g1)
    c: PointOnObject(g12,g11)
    c: Vertical(g12)
    c: Coincident(g13,g2)
    c: PointOnObject(g13,g11)
    c: Vertical(g13)
    c: PointOnObject(g7,g-2)
    c: Coincident(g14,g6)
    c: Coincident(g14,g6)
    c: Coincident(g6,g5)
    c: Coincident(g6,g4)
    c: DistanceY(g0,g2) = 3.6
    c: DistanceY(g-1,g4) = 12
    c: DistanceX(g5,g4) = 32
    c: DistanceX(g0,g0) = 26
    c: DistanceY(g-1,g7) = 40
    c: DistanceY(g8,g7) = 40
    c: Horizontal(g15)
    c: PointOnObject(g16,g7)
    c: Symmetric(g15,g15,g16)
    c: Coincident(g17,g15)
    c: PointOnObject(g17,g3)
    c: Vertical(g17)
    c: Coincident(g18,g17)
    c: PointOnObject(g18,g11)
    c: Coincident(g19,g15)
    c: PointOnObject(g19,g3)
    c: Vertical(g19)
    c: Coincident(g20,g19)
    c: PointOnObject(g20,g11)
    c: DistanceX(g19,g2) = 2.4
    c: DistanceY(g-1,g16) = 2.4
    c: DistanceX(g20,g4) = 2.4
    c: DistanceX(g5,g18) = 2.4
    c: InternalAlignment(g22-g25 -> g21) x4
    c: PointOnObject(g21,g7)
    c: Coincident(g21,g18)
    c: Coincident(g21,g20)
    c: DistanceY(g22,g7) = 2.4
    c: DistanceY(g21,g22) = 40
FEATURE [Sketcher::SketchObject] Sketch017  label="Sketch_EarMicMt_Cut"
  FullyConstrained = true
  MapMode = 5
  Placement = pos=(0,7,1.6e-15) rot=(1,0,0;1.5708rad)
  Support = -> [DatumPlane001]
  expr: Constraints[30] = <<params>>.ear_base_thick + <<params>>.ear_vert_height
  expr: Constraints[31] = <<params>>.ear_gm_mid_height
  expr: Constraints[51] = <<params>>.ear_wall_thick
  expr: Constraints[32] = <<params>>.ear_gm_mid_width
  expr: Constraints[33] = <<params>>.ear_gm_base_width
  expr: Constraints[49] = Spreadsheet.ear_wall_thick
  expr: Constraints[34] = <<params>>.ear_gm_tot_height
  expr: Constraints[50] = Spreadsheet.ear_wall_thick
  expr: Constraints[35] = <<params>>.ear_ellipse_majax
  expr: Constraints[60] = <<params>>.ear_wall_thick
  expr: Constraints[52] = <<params>>.ear_wall_thick
  expr: Constraints[61] = <<params>>.ear_ellipse_majax
  sketch-geometry (26):
    g0: LineSegment StartX=-12.6354 StartY=0 StartZ=0 EndX=12.6354 EndY=0 EndZ=0
    g1: LineSegment StartX=-12.6354 StartY=0 StartZ=0 EndX=-12.6354 EndY=3.6 EndZ=0
    g2: LineSegment StartX=12.6354 StartY=0 StartZ=0 EndX=12.6354 EndY=3.6 EndZ=0
    g3: LineSegment StartX=-12.6354 StartY=3.6 StartZ=0 EndX=12.6354 EndY=3.6 EndZ=0
    g4: LineSegment StartX=12.6354 StartY=3.6 StartZ=0 EndX=14.8333 EndY=10.25 EndZ=0
    g5: LineSegment StartX=-12.6354 StartY=3.6 StartZ=0 EndX=-14.8333 EndY=10.25 EndZ=0
    g6: ArcOfEllipse CenterX=0 CenterY=-7.58333 CenterZ=0 NormalX=0 NormalY=0 NormalZ=1 MajorRadius=40 MinorRadius=16.5714 AngleXU=1.5708 StartAngle=5.17449 EndAngle=7.39188
    g7: LineSegment StartX=0 StartY=32.4167 StartZ=0 EndX=0 EndY=-47.5833 EndZ=0
    g8: LineSegment StartX=-16.5714 StartY=-7.58333 StartZ=0 EndX=16.5714 EndY=-7.58333 EndZ=0
    g9: GeomPoint X=0 Y=28.8226 Z=0
    g10: GeomPoint X=0 Y=-43.9892 Z=0
    g11: LineSegment StartX=-14.8333 StartY=10.25 StartZ=0 EndX=14.8333 EndY=10.25 EndZ=0
    g12: LineSegment StartX=-12.6354 StartY=3.6 StartZ=0 EndX=-12.6354 EndY=10.25 EndZ=0
    g13: LineSegment StartX=12.6354 StartY=3.6 StartZ=0 EndX=12.6354 EndY=10.25 EndZ=0
    g14: LineSegment StartX=-14.8333 StartY=10.25 StartZ=0 EndX=14.8333 EndY=10.25 EndZ=0
    g15: LineSegment StartX=-10.2354 StartY=2.4 StartZ=0 EndX=10.2354 EndY=2.4 EndZ=0
    g16: GeomPoint X=0 Y=2.4 Z=0
    g17: LineSegment StartX=-10.2354 StartY=2.4 StartZ=0 EndX=-10.2354 EndY=3.6 EndZ=0
    g18: LineSegment StartX=-10.2354 StartY=3.6 StartZ=0 EndX=-12.4333 EndY=10.25 EndZ=0
    g19: LineSegment StartX=10.2354 StartY=2.4 StartZ=0 EndX=10.2354 EndY=3.6 EndZ=0
    g20: LineSegment StartX=10.2354 StartY=3.6 StartZ=0 EndX=12.4333 EndY=10.25 EndZ=0
    g21: ArcOfEllipse CenterX=0 CenterY=-9.98333 CenterZ=0 NormalX=0 NormalY=0 NormalZ=1 MajorRadius=40 MinorRadius=14.4133 AngleXU=1.5708 StartAngle=5.24274 EndAngle=7.32363
    g22: LineSegment StartX=-2.9e-15 StartY=30.0167 StartZ=0 EndX=2.9e-15 EndY=-49.9833 EndZ=0
    g23: LineSegment StartX=-14.4133 StartY=-9.98333 StartZ=0 EndX=14.4133 EndY=-9.98333 EndZ=0
    g24: GeomPoint X=-2.8e-15 Y=27.3296 Z=0
    g25: GeomPoint X=2.8e-15 Y=-47.2963 Z=0
  constraints (56):
    c: Horizontal(g0)
    c: Symmetric(g0,g0,g-1)
    c: Coincident(g1,g0)
    c: Vertical(g1)
    c: Coincident(g2,g0)
    c: Vertical(g2)
    c: Coincident(g3,g1)
    c: Coincident(g3,g2)
    c: Horizontal(g3)
    c: Coincident(g4,g2)
    c: Coincident(g5,g1)
    c: InternalAlignment(g7-g10 -> g6) x4
    c: PointOnObject(g6,g-2)
    c: Coincident(g11,g5)
    c: Coincident(g11,g4)
    c: Horizontal(g11)
    c: Coincident(g12,g1)
    c: PointOnObject(g12,g11)
    c: Vertical(g12)
    c: Coincident(g13,g2)
    c: PointOnObject(g13,g11)
    c: Vertical(g13)
    c: PointOnObject(g7,g-2)
    c: Coincident(g14,g6)
    c: Coincident(g14,g6)
    c: Coincident(g6,g5)
    c: Coincident(g6,g4)
    c: DistanceY(g0,g2) = 3.6
    c: DistanceY(g-1,g4) = 10.25
    c: DistanceX(g5,g4) = 29.6667
    c: DistanceX(g0,g0) = 25.2708
    c: DistanceY(g-1,g7) = 32.4167
    c: DistanceY(g8,g7) = 40
    c: Horizontal(g15)
    c: PointOnObject(g16,g7)
    c: Symmetric(g15,g15,g16)
    c: Coincident(g17,g15)
    c: PointOnObject(g17,g3)
    c: Vertical(g17)
    c: Coincident(g18,g17)
    c: PointOnObject(g18,g11)
    c: Coincident(g19,g15)
    c: PointOnObject(g19,g3)
    c: Vertical(g19)
    c: Coincident(g20,g19)
    c: PointOnObject(g20,g11)
    c: DistanceX(g19,g2) = 2.4
    c: DistanceY(g-1,g16) = 2.4
    c: DistanceX(g20,g4) = 2.4
    c: DistanceX(g5,g18) = 2.4
    c: InternalAlignment(g22-g25 -> g21) x4
    c: PointOnObject(g21,g7)
    c: Coincident(g21,g18)
    c: Coincident(g21,g20)
    c: DistanceY(g22,g7) = 2.4
    c: DistanceY(g21,g22) = 40
FEATURE [PartDesign::SubtractiveLoft] SubtractiveLoft
  BaseFeature = -> Pocket007
  Closed = false
  Placement = pos=(0,0,0) rot=(1,0,0;1.5708rad)
  Profile = -> Sketch016
  Ruled = false
  Sections = -> [Sketch017]
FEATURE [Sketcher::SketchObject] Sketch018
  FullyConstrained = true
  MapMode = 5
  Placement = pos=(0,7,1.6e-15) rot=(1,0,0;1.5708rad)
  Support = -> [DatumPlane001]
  expr: Constraints[8] = <<params>>.ear_base_thick + <<params>>.grove_board_width / 2
  expr: Constraints[7] = <<params>>.m2_hole_clear_diam
  expr: Constraints[3] = <<params>>.grove_board_width
  sketch-geometry (4):
    g0: LineSegment StartX=-10 StartY=12 StartZ=0 EndX=10 EndY=12 EndZ=0
    g1: GeomPoint X=0 Y=12 Z=0
    g2: Circle CenterX=-10 CenterY=12 CenterZ=0 NormalX=0 NormalY=0 NormalZ=1 AngleXU=0 Radius=1.25
    g3: Circle CenterX=10 CenterY=12 CenterZ=0 NormalX=0 NormalY=0 NormalZ=1 AngleXU=0 Radius=1.25
  constraints (9):
    c: Horizontal(g0)
    c: PointOnObject(g1,g-2)
    c: Symmetric(g0,g0,g1)
    c: DistanceX(g0,g0) = 20
    c: Coincident(g2,g0)
    c: Coincident(g3,g0)
    c: Equal(g3,g2)
    c: Diameter(g3) = 2.5
    c: DistanceY(g-1,g1) = 12
FEATURE [PartDesign::Pocket] Pocket008  label="Pocket_GroveMtHoles"
  BaseFeature = -> SubtractiveLoft
  Length = 5
  Length2 = 100
  Placement = pos=(0,0,0) rot=(1,0,0;1.5708rad)
  Profile = -> Sketch018
  Type = 1
FEATURE [PartDesign::Plane] DatumPlane002  label="Datum_GroveMicHexOffset"
  AttachmentOffset = pos=(0,0,-10) rot=(0,0,1;0rad)
  Length = 61.2949
  MapMode = 5
  Placement = pos=(0,10,2.2e-15) rot=(1,0,0;1.5708rad)
  ResizeMode = 0
  Support = -> [XZ_Plane001]
  Width = 75.0828
  expr: .AttachmentOffset.Base.z = -1 * (<<params>>.mic_mt_plane_offset_z + <<params>>.mic_mt_hex_offset)
FEATURE [Sketcher::SketchObject] Sketch019
  FullyConstrained = true
  MapMode = 5
  Placement = pos=(0,10,2.2e-15) rot=(1,0,0;1.5708rad)
  Support = -> [DatumPlane002]
  expr: Constraints[44] = <<params>>.ear_base_thick + <<params>>.grove_board_width / 2
  expr: Constraints[43] = <<params>>.m2_nut_clear_flat
  expr: Constraints[3] = <<params>>.grove_board_width
  sketch-geometry (16):
    g0: LineSegment StartX=-10 StartY=12 StartZ=0 EndX=10 EndY=12 EndZ=0
    g1: GeomPoint X=0 Y=12 Z=0
    g2: LineSegment StartX=-10 StartY=14.4249 StartZ=0 EndX=-12.1 EndY=13.2124 EndZ=0
    g3: LineSegment StartX=-12.1 StartY=13.2124 StartZ=0 EndX=-12.1 EndY=10.7876 EndZ=0
    g4: LineSegment StartX=-12.1 StartY=10.7876 StartZ=0 EndX=-10 EndY=9.57513 EndZ=0
    g5: LineSegment StartX=-10 StartY=9.57513 StartZ=0 EndX=-7.9 EndY=10.7876 EndZ=0
    g6: LineSegment StartX=-7.9 StartY=10.7876 StartZ=0 EndX=-7.9 EndY=13.2124 EndZ=0
    g7: LineSegment StartX=-7.9 StartY=13.2124 StartZ=0 EndX=-10 EndY=14.4249 EndZ=0
    g8: Circle CenterX=-10 CenterY=12 CenterZ=0 NormalX=0 NormalY=0 NormalZ=1 AngleXU=0 Radius=2.42487
    g9: LineSegment StartX=10 StartY=14.4249 StartZ=0 EndX=7.9 EndY=13.2124 EndZ=0
    g10: LineSegment StartX=7.9 StartY=13.2124 StartZ=0 EndX=7.9 EndY=10.7876 EndZ=0
    g11: LineSegment StartX=7.9 StartY=10.7876 StartZ=0 EndX=10 EndY=9.57513 EndZ=0
    g12: LineSegment StartX=10 StartY=9.57513 StartZ=0 EndX=12.1 EndY=10.7876 EndZ=0
    g13: LineSegment StartX=12.1 StartY=10.7876 StartZ=0 EndX=12.1 EndY=13.2124 EndZ=0
    g14: LineSegment StartX=12.1 StartY=13.2124 StartZ=0 EndX=10 EndY=14.4249 EndZ=0
    g15: Circle CenterX=10 CenterY=12 CenterZ=0 NormalX=0 NormalY=0 NormalZ=1 AngleXU=0 Radius=2.42487
  constraints (37):
    c: Horizontal(g0)
    c: PointOnObject(g1,g-2)
    c: Symmetric(g0,g0,g1)
    c: DistanceX(g0,g0) = 20
    c: Coincident(g2,g3)
    c: Coincident(g3,g4)
    c: Coincident(g4,g5)
    c: Coincident(g5,g6)
    c: Coincident(g6,g7)
    c: Coincident(g7,g2)
    c: Equal(g2, g3-g7) x5
    c: PointOnObject(g2,g8)
    c: PointOnObject(g3,g8)
    c: PointOnObject(g4,g8)
    c: PointOnObject(g5,g8)
    c: PointOnObject(g6,g8)
    c: PointOnObject(g7,g8)
    c: Coincident(g8,g0)
    c: Coincident(g9,g10)
    c: Coincident(g10,g11)
    c: Coincident(g11,g12)
    c: Coincident(g12,g13)
    c: Coincident(g13,g14)
    c: Coincident(g14,g9)
    c: Equal(g9, g10-g14) x5
    c: PointOnObject(g9,g15)
    c: PointOnObject(g10,g15)
    c: PointOnObject(g11,g15)
    c: PointOnObject(g12,g15)
    c: PointOnObject(g13,g15)
    c: PointOnObject(g14,g15)
    c: Coincident(g15,g0)
    c: Equal(g8,g15)
    c: Vertical(g6)
    c: Vertical(g10)
    c: DistanceX(g9,g13) = 4.2
    c: DistanceY(g-1,g1) = 12
FEATURE [PartDesign::Pocket] Pocket009  label="Pocket_GroveMicHexSunk"
  BaseFeature = -> Pocket008
  Length = 5
  Length2 = 100
  Placement = pos=(0,0,0) rot=(1,0,0;1.5708rad)
  Profile = -> Sketch019
  Type = 1
FEATURE [Sketcher::SketchObject] Sketch020  label="Sketch_EarTrimFr"
  FullyConstrained = true
  MapMode = 5
  Placement = pos=(0,0,0) rot=(1,0,0;1.5708rad)
  Support = -> [XZ_Plane009]
  expr: Constraints[30] = <<params>>.ear_base_thick + <<params>>.ear_vert_height
  expr: Constraints[31] = <<params>>.ear_front_mid_height
  expr: Constraints[32] = <<params>>.ear_front_mid_width
  expr: Constraints[33] = <<params>>.ear_front_base_width
  expr: Constraints[45] = <<params>>.ear_trim_thick
  expr: Constraints[34] = <<params>>.ear_front_tot_height
  expr: Constraints[35] = <<params>>.ear_ellipse_majax
  expr: Constraints[40] = <<params>>.ear_ellipse_majax
  expr: Constraints[46] = <<params>>.ear_trim_thick
  expr: Constraints[55] = <<params>>.ear_ellipse_majax
  sketch-geometry (27):
    g0: LineSegment StartX=-13 StartY=0 StartZ=0 EndX=13 EndY=0 EndZ=0
    g1: LineSegment StartX=-13 StartY=0 StartZ=0 EndX=-13 EndY=3.6 EndZ=0
    g2: LineSegment StartX=13 StartY=0 StartZ=0 EndX=13 EndY=3.6 EndZ=0
    g3: LineSegment StartX=-13 StartY=3.6 StartZ=0 EndX=13 EndY=3.6 EndZ=0
    g4: LineSegment StartX=13 StartY=3.6 StartZ=0 EndX=16 EndY=12 EndZ=0
    g5: LineSegment StartX=-13 StartY=3.6 StartZ=0 EndX=-16 EndY=12 EndZ=0
    g6: ArcOfEllipse CenterX=0 CenterY=-1.9e-15 CenterZ=0 NormalX=0 NormalY=0 NormalZ=1 MajorRadius=40 MinorRadius=16.7726 AngleXU=1.5708 StartAngle=5.01708 EndAngle=7.54929
    g7: LineSegment StartX=0 StartY=40 StartZ=0 EndX=0 EndY=-40 EndZ=0
    g8: LineSegment StartX=-16.7726 StartY=-1.9e-15 StartZ=0 EndX=16.7726 EndY=-1.9e-15 EndZ=0
    g9: GeomPoint X=0 Y=36.3137 Z=0
    g10: GeomPoint X=0 Y=-36.3137 Z=0
    g11: LineSegment StartX=-16 StartY=12 StartZ=0 EndX=16 EndY=12 EndZ=0
    g12: LineSegment StartX=-13 StartY=3.6 StartZ=0 EndX=-13 EndY=12 EndZ=0
    g13: LineSegment StartX=13 StartY=3.6 StartZ=0 EndX=13 EndY=12 EndZ=0
    g14: LineSegment StartX=-16 StartY=12 StartZ=0 EndX=16 EndY=12 EndZ=0
    g15: ArcOfEllipse CenterX=0 CenterY=-1.2 CenterZ=0 NormalX=0 NormalY=0 NormalZ=1 MajorRadius=40 MinorRadius=15.6783 AngleXU=1.5708 StartAngle=5.04869 EndAngle=7.51768
    g16: LineSegment StartX=0 StartY=38.8 StartZ=0 EndX=0 EndY=-41.2 EndZ=0
    g17: LineSegment StartX=-15.6783 StartY=-1.2 StartZ=0 EndX=15.6783 EndY=-1.2 EndZ=0
    g18: GeomPoint X=0 Y=35.5993 Z=0
    g19: GeomPoint X=0 Y=-37.9993 Z=0
    g20: LineSegment StartX=-14.8 StartY=12 StartZ=0 EndX=-16 EndY=12 EndZ=0
    g21: LineSegment StartX=14.8 StartY=12 StartZ=0 EndX=16 EndY=12 EndZ=0
    g22: ArcOfEllipse CenterX=3e-16 CenterY=-3e-16 CenterZ=0 NormalX=0 NormalY=0 NormalZ=1 MajorRadius=40 MinorRadius=16.7726 AngleXU=1.5708 StartAngle=5.01708 EndAngle=7.54929
    g23: LineSegment StartX=0 StartY=40 StartZ=0 EndX=6e-16 EndY=-40 EndZ=0
    g24: LineSegment StartX=-16.7726 StartY=-4e-16 StartZ=0 EndX=16.7726 EndY=-2e-16 EndZ=0
    g25: GeomPoint X=0 Y=36.3137 Z=0
    g26: GeomPoint X=6e-16 Y=-36.3137 Z=0
  constraints (50):
    c: Horizontal(g0)
    c: Symmetric(g0,g0,g-1)
    c: Coincident(g1,g0)
    c: Vertical(g1)
    c: Coincident(g2,g0)
    c: Vertical(g2)
    c: Coincident(g3,g1)
    c: Coincident(g3,g2)
    c: Horizontal(g3)
    c: Coincident(g4,g2)
    c: Coincident(g5,g1)
    c: InternalAlignment(g7-g10 -> g6) x4
    c: PointOnObject(g6,g-2)
    c: Coincident(g11,g5)
    c: Coincident(g11,g4)
    c: Horizontal(g11)
    c: Coincident(g12,g1)
    c: PointOnObject(g12,g11)
    c: Vertical(g12)
    c: Coincident(g13,g2)
    c: PointOnObject(g13,g11)
    c: Vertical(g13)
    c: PointOnObject(g7,g-2)
    c: Coincident(g14,g6)
    c: Coincident(g14,g6)
    c: Coincident(g6,g5)
    c: Coincident(g6,g4)
    c: DistanceY(g0,g2) = 3.6
    c: DistanceY(g-1,g4) = 12
    c: DistanceX(g5,g4) = 32
    c: DistanceX(g0,g0) = 26
    c: DistanceY(g-1,g7) = 40
    c: DistanceY(g8,g7) = 40
    c: InternalAlignment(g16-g19 -> g15) x4
    c: DistanceY(g17,g16) = 40
    c: Vertical(g16)
    c: PointOnObject(g16,g-2)
    c: PointOnObject(g15,g11)
    c: PointOnObject(g15,g11)
    c: DistanceX(g15,g4) = 1.2
    c: DistanceY(g16,g7) = 1.2
    c: Coincident(g20,g15)
    c: Coincident(g20,g5)
    c: Coincident(g21,g15)
    c: Coincident(g21,g4)
    c: InternalAlignment(g23-g26 -> g22) x4
    c: DistanceY(g22,g23) = 40
    c: Coincident(g22,g20)
    c: Coincident(g22,g21)
    c: Coincident(g23,g7)
FEATURE [PartDesign::Plane] DatumPlane003  label="Datum_EarTrimBack"
  AttachmentOffset = pos=(0,0,-4) rot=(0,0,1;0rad)
  Length = 61.3994
  MapMode = 5
  Placement = pos=(0,4,9e-16) rot=(1,0,0;1.5708rad)
  ResizeMode = 0
  Support = -> [XZ_Plane009]
  Width = 76.373
  expr: .AttachmentOffset.Base.z = -1 * <<params>>.ear_trim_leng
FEATURE [Sketcher::SketchObject] Sketch021  label="Sketch_EarTrimBk"
  FullyConstrained = true
  MapMode = 5
  Placement = pos=(0,4,9e-16) rot=(1,0,0;1.5708rad)
  Support = -> [DatumPlane003]
  expr: Constraints[55] = <<params>>.ear_ellipse_majax
  expr: Constraints[46] = <<params>>.ear_trim_thick
  expr: Constraints[40] = <<params>>.ear_ellipse_majax
  expr: Constraints[35] = <<params>>.ear_ellipse_majax
  expr: Constraints[34] = <<params>>.ear_trim_tot_height
  expr: Constraints[45] = <<params>>.ear_trim_thick
  expr: Constraints[33] = <<params>>.ear_trim_base_width
  expr: Constraints[32] = <<params>>.ear_trim_mid_width
  expr: Constraints[31] = <<params>>.ear_trim_mid_height
  expr: Constraints[30] = <<params>>.ear_base_thick + <<params>>.ear_vert_height
  sketch-geometry (27):
    g0: LineSegment StartX=-12.7917 StartY=0 StartZ=0 EndX=12.7917 EndY=0 EndZ=0
    g1: LineSegment StartX=-12.7917 StartY=0 StartZ=0 EndX=-12.7917 EndY=3.6 EndZ=0
    g2: LineSegment StartX=12.7917 StartY=0 StartZ=0 EndX=12.7917 EndY=3.6 EndZ=0
    g3: LineSegment StartX=-12.7917 StartY=3.6 StartZ=0 EndX=12.7917 EndY=3.6 EndZ=0
    g4: LineSegment StartX=12.7917 StartY=3.6 StartZ=0 EndX=15.3333 EndY=11 EndZ=0
    g5: LineSegment StartX=-12.7917 StartY=3.6 StartZ=0 EndX=-15.3333 EndY=11 EndZ=0
    g6: ArcOfEllipse CenterX=0 CenterY=-4.33333 CenterZ=0 NormalX=0 NormalY=0 NormalZ=1 MajorRadius=40 MinorRadius=16.6015 AngleXU=1.5708 StartAngle=5.10579 EndAngle=7.46058
    g7: LineSegment StartX=0 StartY=35.6667 StartZ=0 EndX=0 EndY=-44.3333 EndZ=0
    g8: LineSegment StartX=-16.6015 StartY=-4.33333 StartZ=0 EndX=16.6015 EndY=-4.33333 EndZ=0
    g9: GeomPoint X=0 Y=32.0588 Z=0
    g10: GeomPoint X=0 Y=-40.7255 Z=0
    g11: LineSegment StartX=-15.3333 StartY=11 StartZ=0 EndX=15.3333 EndY=11 EndZ=0
    g12: LineSegment StartX=-12.7917 StartY=3.6 StartZ=0 EndX=-12.7917 EndY=11 EndZ=0
    g13: LineSegment StartX=12.7917 StartY=3.6 StartZ=0 EndX=12.7917 EndY=11 EndZ=0
    g14: LineSegment StartX=-15.3333 StartY=11 StartZ=0 EndX=15.3333 EndY=11 EndZ=0
    g15: ArcOfEllipse CenterX=0 CenterY=-5.53333 CenterZ=0 NormalX=0 NormalY=0 NormalZ=1 MajorRadius=40 MinorRadius=15.5212 AngleXU=1.5708 StartAngle=5.1385 EndAngle=7.42787
    g16: LineSegment StartX=0 StartY=34.4667 StartZ=0 EndX=0 EndY=-45.5333 EndZ=0
    g17: LineSegment StartX=-15.5212 StartY=-5.53333 StartZ=0 EndX=15.5212 EndY=-5.53333 EndZ=0
    g18: GeomPoint X=0 Y=31.3325 Z=0
    g19: GeomPoint X=0 Y=-42.3992 Z=0
    g20: LineSegment StartX=-14.1333 StartY=11 StartZ=0 EndX=-15.3333 EndY=11 EndZ=0
    g21: LineSegment StartX=14.1333 StartY=11 StartZ=0 EndX=15.3333 EndY=11 EndZ=0
    g22: ArcOfEllipse CenterX=0 CenterY=-4.33333 CenterZ=0 NormalX=0 NormalY=0 NormalZ=1 MajorRadius=40 MinorRadius=16.6015 AngleXU=1.5708 StartAngle=5.10579 EndAngle=7.46058
    g23: LineSegment StartX=0 StartY=35.6667 StartZ=0 EndX=-1e-16 EndY=-44.3333 EndZ=0
    g24: LineSegment StartX=-16.6015 StartY=-4.33333 StartZ=0 EndX=16.6015 EndY=-4.33333 EndZ=0
    g25: GeomPoint X=0 Y=32.0588 Z=0
    g26: GeomPoint X=-1e-16 Y=-40.7255 Z=0
  constraints (50):
    c: Horizontal(g0)
    c: Symmetric(g0,g0,g-1)
    c: Coincident(g1,g0)
    c: Vertical(g1)
    c: Coincident(g2,g0)
    c: Vertical(g2)
    c: Coincident(g3,g1)
    c: Coincident(g3,g2)
    c: Horizontal(g3)
    c: Coincident(g4,g2)
    c: Coincident(g5,g1)
    c: InternalAlignment(g7-g10 -> g6) x4
    c: PointOnObject(g6,g-2)
    c: Coincident(g11,g5)
    c: Coincident(g11,g4)
    c: Horizontal(g11)
    c: Coincident(g12,g1)
    c: PointOnObject(g12,g11)
    c: Vertical(g12)
    c: Coincident(g13,g2)
    c: PointOnObject(g13,g11)
    c: Vertical(g13)
    c: PointOnObject(g7,g-2)
    c: Coincident(g14,g6)
    c: Coincident(g14,g6)
    c: Coincident(g6,g5)
    c: Coincident(g6,g4)
    c: DistanceY(g0,g2) = 3.6
    c: DistanceY(g-1,g4) = 11
    c: DistanceX(g5,g4) = 30.6667
    c: DistanceX(g0,g0) = 25.5833
    c: DistanceY(g-1,g7) = 35.6667
    c: DistanceY(g8,g7) = 40
    c: InternalAlignment(g16-g19 -> g15) x4
    c: DistanceY(g17,g16) = 40
    c: Vertical(g16)
    c: PointOnObject(g16,g-2)
    c: PointOnObject(g15,g11)
    c: PointOnObject(g15,g11)
    c: DistanceX(g15,g4) = 1.2
    c: DistanceY(g16,g7) = 1.2
    c: Coincident(g20,g15)
    c: Coincident(g20,g5)
    c: Coincident(g21,g15)
    c: Coincident(g21,g4)
    c: InternalAlignment(g23-g26 -> g22) x4
    c: DistanceY(g22,g23) = 40
    c: Coincident(g22,g20)
    c: Coincident(g22,g21)
    c: Coincident(g23,g7)
FEATURE [PartDesign::Plane] DatumPlane004  label="Datum_EarTrim"
  AttachmentOffset = pos=(0,0,-4) rot=(0,0,1;0rad)
  Length = 61.2949
  MapMode = 5
  Placement = pos=(0,4,9e-16) rot=(1,0,0;1.5708rad)
  ResizeMode = 0
  Support = -> [XZ_Plane001]
  Width = 75.0828
  expr: .AttachmentOffset.Base.z = -1 * <<params>>.ear_trim_leng
FEATURE [Sketcher::SketchObject] Sketch022  label="Sketch_EarTrimF"
  FullyConstrained = true
  MapMode = 5
  Placement = pos=(0,0,0) rot=(1,0,0;1.5708rad)
  Support = -> [XZ_Plane001]
  expr: Constraints[64] = <<params>>.ear_trim_thick
  expr: Constraints[47] = <<params>>.ear_trim_thick
  expr: Constraints[46] = <<params>>.ear_trim_thick
  expr: Constraints[30] = <<params>>.ear_base_thick + <<params>>.ear_vert_height
  expr: Constraints[31] = <<params>>.ear_front_mid_height
  expr: Constraints[32] = <<params>>.ear_front_mid_width
  expr: Constraints[48] = <<params>>.ear_ellipse_majax
  expr: Constraints[33] = <<params>>.ear_front_base_width
  expr: Constraints[34] = <<params>>.ear_front_tot_height
  expr: Constraints[35] = <<params>>.ear_ellipse_majax
  sketch-geometry (27):
    g0: LineSegment StartX=-13 StartY=0 StartZ=0 EndX=13 EndY=0 EndZ=0
    g1: LineSegment StartX=-13 StartY=0 StartZ=0 EndX=-13 EndY=3.6 EndZ=0
    g2: LineSegment StartX=13 StartY=0 StartZ=0 EndX=13 EndY=3.6 EndZ=0
    g3: LineSegment StartX=-13 StartY=3.6 StartZ=0 EndX=13 EndY=3.6 EndZ=0
    g4: LineSegment StartX=13 StartY=3.6 StartZ=0 EndX=16 EndY=12 EndZ=0
    g5: LineSegment StartX=-13 StartY=3.6 StartZ=0 EndX=-16 EndY=12 EndZ=0
    g6: ArcOfEllipse CenterX=0 CenterY=-3.2e-15 CenterZ=0 NormalX=0 NormalY=0 NormalZ=1 MajorRadius=40 MinorRadius=16.7726 AngleXU=1.5708 StartAngle=5.01708 EndAngle=7.54929
    g7: LineSegment StartX=0 StartY=40 StartZ=0 EndX=0 EndY=-40 EndZ=0
    g8: LineSegment StartX=-16.7726 StartY=-3.2e-15 StartZ=0 EndX=16.7726 EndY=-3.2e-15 EndZ=0
    g9: GeomPoint X=0 Y=36.3137 Z=0
    g10: GeomPoint X=0 Y=-36.3137 Z=0
    g11: LineSegment StartX=-16 StartY=12 StartZ=0 EndX=16 EndY=12 EndZ=0
    g12: LineSegment StartX=-13 StartY=3.6 StartZ=0 EndX=-13 EndY=12 EndZ=0
    g13: LineSegment StartX=13 StartY=3.6 StartZ=0 EndX=13 EndY=12 EndZ=0
    g14: LineSegment StartX=-16 StartY=12 StartZ=0 EndX=16 EndY=12 EndZ=0
    g15: ArcOfEllipse CenterX=-1.7e-15 CenterY=-1.2 CenterZ=0 NormalX=0 NormalY=0 NormalZ=1 MajorRadius=40 MinorRadius=15.6783 AngleXU=1.5708 StartAngle=5.04869 EndAngle=7.51768
    g16: LineSegment StartX=-1.7e-15 StartY=38.8 StartZ=0 EndX=-1.7e-15 EndY=-41.2 EndZ=0
    g17: LineSegment StartX=-15.6783 StartY=-1.2 StartZ=0 EndX=15.6783 EndY=-1.2 EndZ=0
    g18: GeomPoint X=-1.7e-15 Y=35.5993 Z=0
    g19: GeomPoint X=-1.7e-15 Y=-37.9993 Z=0
    g20: LineSegment StartX=-16 StartY=12 StartZ=0 EndX=-14.8 EndY=12 EndZ=0
    g21: LineSegment StartX=16 StartY=12 StartZ=0 EndX=14.8 EndY=12 EndZ=0
    g22: LineSegment StartX=-16 StartY=12 StartZ=0 EndX=-17.2 EndY=12 EndZ=0
    g23: LineSegment StartX=16 StartY=12 StartZ=0 EndX=17.2 EndY=12 EndZ=0
    g24: LineSegment StartX=17.2 StartY=12 StartZ=0 EndX=17.2 EndY=41.2 EndZ=0
    g25: LineSegment StartX=17.2 StartY=41.2 StartZ=0 EndX=-17.2 EndY=41.2 EndZ=0
    g26: LineSegment StartX=-17.2 StartY=41.2 StartZ=0 EndX=-17.2 EndY=12 EndZ=0
  constraints (59):
    c: Horizontal(g0)
    c: Symmetric(g0,g0,g-1)
    c: Coincident(g1,g0)
    c: Vertical(g1)
    c: Coincident(g2,g0)
    c: Vertical(g2)
    c: Coincident(g3,g1)
    c: Coincident(g3,g2)
    c: Horizontal(g3)
    c: Coincident(g4,g2)
    c: Coincident(g5,g1)
    c: InternalAlignment(g7-g10 -> g6) x4
    c: PointOnObject(g6,g-2)
    c: Coincident(g11,g5)
    c: Coincident(g11,g4)
    c: Horizontal(g11)
    c: Coincident(g12,g1)
    c: PointOnObject(g12,g11)
    c: Vertical(g12)
    c: Coincident(g13,g2)
    c: PointOnObject(g13,g11)
    c: Vertical(g13)
    c: PointOnObject(g7,g-2)
    c: Coincident(g14,g6)
    c: Coincident(g14,g6)
    c: Coincident(g6,g5)
    c: Coincident(g6,g4)
    c: DistanceY(g0,g2) = 3.6
    c: DistanceY(g-1,g4) = 12
    c: DistanceX(g5,g4) = 32
    c: DistanceX(g0,g0) = 26
    c: DistanceY(g-1,g7) = 40
    c: DistanceY(g8,g7) = 40
    c: InternalAlignment(g16-g19 -> g15) x4
    c: Vertical(g16)
    c: PointOnObject(g20,g11)
    c: PointOnObject(g21,g11)
    c: Coincident(g15,g20)
    c: Coincident(g15,g21)
    c: Equal(g21,g20)
    c: DistanceX(g15,g4) = 1.2
    c: DistanceY(g16,g7) = 1.2
    c: DistanceY(g17,g16) = 40
    c: Coincident(g22,g20)
    c: Horizontal(g22)
    c: Coincident(g23,g21)
    c: Horizontal(g23)
    c: Coincident(g24,g23)
    c: Vertical(g24)
    c: Coincident(g25,g24)
    c: Horizontal(g25)
    c: Coincident(g26,g25)
    c: Coincident(g26,g22)
    c: Vertical(g26)
    c: Equal(g21,g23)
    c: Equal(g20,g22)
    c: Coincident(g20,g5)
    c: Coincident(g21,g4)
    c: DistanceY(g7,g24) = 1.2
FEATURE [Sketcher::SketchObject] Sketch023  label="Sketch_EarTrimB"
  FullyConstrained = true
  MapMode = 5
  Placement = pos=(0,4,9e-16) rot=(1,0,0;1.5708rad)
  Support = -> [DatumPlane004]
  expr: Constraints[32] = <<params>>.ear_trim_mid_width
  expr: Constraints[64] = <<params>>.ear_trim_thick
  expr: Constraints[35] = <<params>>.ear_ellipse_majax
  expr: Constraints[34] = <<params>>.ear_trim_tot_height
  expr: Constraints[33] = <<params>>.ear_front_base_width
  expr: Constraints[48] = <<params>>.ear_ellipse_majax
  expr: Constraints[31] = <<params>>.ear_trim_mid_height
  expr: Constraints[30] = <<params>>.ear_base_thick + <<params>>.ear_vert_height
  expr: Constraints[46] = <<params>>.ear_trim_thick
  expr: Constraints[47] = <<params>>.ear_trim_thick
  sketch-geometry (27):
    g0: LineSegment StartX=-13 StartY=0 StartZ=0 EndX=13 EndY=0 EndZ=0
    g1: LineSegment StartX=-13 StartY=0 StartZ=0 EndX=-13 EndY=3.6 EndZ=0
    g2: LineSegment StartX=13 StartY=0 StartZ=0 EndX=13 EndY=3.6 EndZ=0
    g3: LineSegment StartX=-13 StartY=3.6 StartZ=0 EndX=13 EndY=3.6 EndZ=0
    g4: LineSegment StartX=13 StartY=3.6 StartZ=0 EndX=15.3333 EndY=11 EndZ=0
    g5: LineSegment StartX=-13 StartY=3.6 StartZ=0 EndX=-15.3333 EndY=11 EndZ=0
    g6: ArcOfEllipse CenterX=0 CenterY=-4.33333 CenterZ=0 NormalX=0 NormalY=0 NormalZ=1 MajorRadius=40 MinorRadius=16.6015 AngleXU=1.5708 StartAngle=5.10579 EndAngle=7.46058
    g7: LineSegment StartX=0 StartY=35.6667 StartZ=0 EndX=0 EndY=-44.3333 EndZ=0
    g8: LineSegment StartX=-16.6015 StartY=-4.33333 StartZ=0 EndX=16.6015 EndY=-4.33333 EndZ=0
    g9: GeomPoint X=0 Y=32.0588 Z=0
    g10: GeomPoint X=0 Y=-40.7255 Z=0
    g11: LineSegment StartX=-15.3333 StartY=11 StartZ=0 EndX=15.3333 EndY=11 EndZ=0
    g12: LineSegment StartX=-13 StartY=3.6 StartZ=0 EndX=-13 EndY=11 EndZ=0
    g13: LineSegment StartX=13 StartY=3.6 StartZ=0 EndX=13 EndY=11 EndZ=0
    g14: LineSegment StartX=-15.3333 StartY=11 StartZ=0 EndX=15.3333 EndY=11 EndZ=0
    g15: ArcOfEllipse CenterX=-2.9e-15 CenterY=-5.53333 CenterZ=0 NormalX=0 NormalY=0 NormalZ=1 MajorRadius=40 MinorRadius=15.5212 AngleXU=1.5708 StartAngle=5.1385 EndAngle=7.42787
    g16: LineSegment StartX=-2.9e-15 StartY=34.4667 StartZ=0 EndX=-2.9e-15 EndY=-45.5333 EndZ=0
    g17: LineSegment StartX=-15.5212 StartY=-5.53333 StartZ=0 EndX=15.5212 EndY=-5.53333 EndZ=0
    g18: GeomPoint X=-2.9e-15 Y=31.3325 Z=0
    g19: GeomPoint X=-2.9e-15 Y=-42.3992 Z=0
    g20: LineSegment StartX=-15.3333 StartY=11 StartZ=0 EndX=-14.1333 EndY=11 EndZ=0
    g21: LineSegment StartX=15.3333 StartY=11 StartZ=0 EndX=14.1333 EndY=11 EndZ=0
    g22: LineSegment StartX=15.3333 StartY=11 StartZ=0 EndX=16.5333 EndY=11 EndZ=0
    g23: LineSegment StartX=16.5333 StartY=11 StartZ=0 EndX=16.5333 EndY=36.8667 EndZ=0
    g24: LineSegment StartX=16.5333 StartY=36.8667 StartZ=0 EndX=-16.5333 EndY=36.8667 EndZ=0
    g25: LineSegment StartX=-16.5333 StartY=36.8667 StartZ=0 EndX=-16.5333 EndY=11 EndZ=0
    g26: LineSegment StartX=-16.5333 StartY=11 StartZ=0 EndX=-15.3333 EndY=11 EndZ=0
  constraints (59):
    c: Horizontal(g0)
    c: Symmetric(g0,g0,g-1)
    c: Coincident(g1,g0)
    c: Vertical(g1)
    c: Coincident(g2,g0)
    c: Vertical(g2)
    c: Coincident(g3,g1)
    c: Coincident(g3,g2)
    c: Horizontal(g3)
    c: Coincident(g4,g2)
    c: Coincident(g5,g1)
    c: InternalAlignment(g7-g10 -> g6) x4
    c: PointOnObject(g6,g-2)
    c: Coincident(g11,g5)
    c: Coincident(g11,g4)
    c: Horizontal(g11)
    c: Coincident(g12,g1)
    c: PointOnObject(g12,g11)
    c: Vertical(g12)
    c: Coincident(g13,g2)
    c: PointOnObject(g13,g11)
    c: Vertical(g13)
    c: PointOnObject(g7,g-2)
    c: Coincident(g14,g6)
    c: Coincident(g14,g6)
    c: Coincident(g6,g5)
    c: Coincident(g6,g4)
    c: DistanceY(g0,g2) = 3.6
    c: DistanceY(g-1,g4) = 11
    c: DistanceX(g5,g4) = 30.6667
    c: DistanceX(g0,g0) = 26
    c: DistanceY(g-1,g7) = 35.6667
    c: DistanceY(g8,g7) = 40
    c: InternalAlignment(g16-g19 -> g15) x4
    c: Vertical(g16)
    c: PointOnObject(g20,g11)
    c: PointOnObject(g21,g11)
    c: Coincident(g15,g20)
    c: Coincident(g15,g21)
    c: Equal(g21,g20)
    c: DistanceX(g15,g4) = 1.2
    c: DistanceY(g16,g7) = 1.2
    c: DistanceY(g17,g16) = 40
    c: Coincident(g22,g21)
    c: Horizontal(g22)
    c: Coincident(g23,g22)
    c: Vertical(g23)
    c: Coincident(g24,g23)
    c: Horizontal(g24)
    c: Coincident(g25,g24)
    c: Vertical(g25)
    c: Coincident(g26,g25)
    c: Coincident(g26,g20)
    c: Horizontal(g26)
    c: Equal(g20,g26)
    c: Coincident(g20,g5)
    c: Equal(g22,g21)
    c: Coincident(g21,g4)
    c: DistanceY(g7,g23) = 1.2
FEATURE [PartDesign::SubtractiveLoft] SubtractiveLoft001  label="SubtractiveLoft_EarTrim"
  BaseFeature = -> Pocket009
  Closed = false
  Placement = pos=(0,0,0) rot=(1,0,0;1.5708rad)
  Profile = -> Sketch022
  Ruled = false
  Sections = -> [Sketch023]
FEATURE [Sketcher::SketchObject] Sketch024  label="Sketch_ClipHole"
  FullyConstrained = true
  MapMode = 5
  Placement = pos=(0,0,0) rot=(0.57735,0.57735,0.57735;2.0944rad)
  Support = -> [YZ_Plane001]
  expr: Constraints[9] = <<params>>.ear_trim_clip_height + <<params>>.ear_trim_clip_tol
  expr: Constraints[10] = Spreadsheet.ear_trim_clip_width + <<params>>.ear_trim_clip_tol
  expr: Constraints[11] = <<params>>.ear_trim_leng
  expr: Constraints[12] = <<params>>.ear_front_mid_height + <<params>>.ear_trim_clip_height + <<params>>.ear_trim_clip_tol / 2
  sketch-geometry (5):
    g0: LineSegment StartX=2.2 StartY=16.7 StartZ=0 EndX=4 EndY=16.7 EndZ=0
    g1: LineSegment StartX=4 StartY=16.7 StartZ=0 EndX=4 EndY=13.5 EndZ=0
    g2: LineSegment StartX=4 StartY=13.5 StartZ=0 EndX=2.2 EndY=13.5 EndZ=0
    g3: LineSegment StartX=2.2 StartY=13.5 StartZ=0 EndX=2.2 EndY=16.7 EndZ=0
    g4: GeomPoint X=3.1 Y=15.1 Z=0
  constraints (13):
    c: Coincident(g0,g1)
    c: Coincident(g1,g2)
    c: Coincident(g2,g3)
    c: Coincident(g3,g0)
    c: Horizontal(g0)
    c: Horizontal(g2)
    c: Vertical(g1)
    c: Vertical(g3)
    c: Symmetric(g2,g0,g4)
    c: DistanceY(g2,g0) = 3.2
    c: DistanceX(g2,g1) = 1.8
    c: DistanceX(g-1,g0) = 4
    c: DistanceY(g-1,g4) = 15.1
FEATURE [PartDesign::Pocket] Pocket010  label="Pocket_EarTrimMtSlot"
  BaseFeature = -> SubtractiveLoft001
  Length = 5
  Length2 = 100
  Midplane = true
  Placement = pos=(0,0,0) rot=(1,0,0;1.5708rad)
  Profile = -> Sketch024
  Type = 1
FEATURE [PartDesign::Body] Body  label="EarMt"
  Group = -> [DatumPlane,Sketch,Sketch001,AdditiveLoft,Sketch002,Pocket,Sketch003,Sketch004,DatumPlane001,Sketch015,Pocket007,Sketch016,Sketch017,SubtractiveLoft,Sketch018,Pocket008,DatumPlane002,Sketch019,Pocket009,DatumPlane004,Sketch022,Sketch023,SubtractiveLoft001,Sketch024,Pocket010]
  Origin = -> Origin001
  Tip = -> Pocket010
FEATURE [PartDesign::AdditiveLoft] AdditiveLoft001  label="AdditiveLoft_EarTrimMain"
  Closed = false
  Placement = pos=(0,0,0) rot=(1,0,0;1.5708rad)
  Profile = -> Sketch020
  Ruled = false
  Sections = -> [Sketch021]
FEATURE [Sketcher::SketchObject] Sketch025  label="Sketch_ClipSplit_Top"
  FullyConstrained = true
  MapMode = 5
  Placement = pos=(0,0,0) rot=(0.57735,0.57735,0.57735;2.0944rad)
  Support = -> [YZ_Plane009]
  expr: Constraints[8] = <<params>>.ear_trim_leng
  expr: Constraints[25] = <<params>>.ear_front_mid_height + <<params>>.ear_trim_clip_height + <<params>>.ear_trim_clip_tol / 2
  expr: Constraints[28] = <<params>>.ear_trim_clip_thick + <<params>>.ear_trim_clip_wedge_size
  expr: Constraints[26] = <<params>>.ear_trim_clip_width
  expr: Constraints[27] = <<params>>.ear_trim_clip_height - 2 * <<params>>.ear_trim_clip_thick
  sketch-geometry (11):
    g0: LineSegment StartX=2.4 StartY=17 StartZ=0 EndX=4 EndY=17 EndZ=0
    g1: LineSegment StartX=4 StartY=17 StartZ=0 EndX=4 EndY=15.8 EndZ=0
    g2: LineSegment StartX=4 StartY=15.8 StartZ=0 EndX=2.4 EndY=15.8 EndZ=0
    g3: LineSegment StartX=2.4 StartY=15.8 StartZ=0 EndX=2.4 EndY=17 EndZ=0
    g4: GeomPoint X=3.2 Y=15.1 Z=0
    g5: LineSegment StartX=2.4 StartY=14.4 StartZ=0 EndX=4 EndY=14.4 EndZ=0
    g6: LineSegment StartX=4 StartY=14.4 StartZ=0 EndX=4 EndY=13.2 EndZ=0
    g7: LineSegment StartX=4 StartY=13.2 StartZ=0 EndX=2.4 EndY=13.2 EndZ=0
    g8: LineSegment StartX=2.4 StartY=13.2 StartZ=0 EndX=2.4 EndY=14.4 EndZ=0
    g9: LineSegment StartX=2.4 StartY=15.8 StartZ=0 EndX=2.4 EndY=14.4 EndZ=0
    g10: LineSegment StartX=4 StartY=15.8 StartZ=0 EndX=4 EndY=14.4 EndZ=0
  constraints (29):
    c: Coincident(g0,g1)
    c: Coincident(g1,g2)
    c: Coincident(g2,g3)
    c: Coincident(g3,g0)
    c: Horizontal(g0)
    c: Horizontal(g2)
    c: Vertical(g1)
    c: Vertical(g3)
    c: DistanceX(g-1,g1) = 4
    c: Coincident(g5,g6)
    c: Coincident(g6,g7)
    c: Coincident(g7,g8)
    c: Coincident(g8,g5)
    c: Horizontal(g5)
    c: Horizontal(g7)
    c: Vertical(g6)
    c: Vertical(g8)
    c: Coincident(g9,g2)
    c: Coincident(g9,g5)
    c: Coincident(g10,g1)
    c: Coincident(g10,g5)
    c: Vertical(g10)
    c: Vertical(g9)
    c: Symmetric(g1,g5,g4)
    c: Equal(g3,g8)
    c: DistanceY(g-1,g4) = 15.1
    c: DistanceX(g7,g6) = 1.6
    c: DistanceY(g5,g1) = 1.4
    c: DistanceY(g1,g0) = 1.2
FEATURE [PartDesign::Pad] Pad009  label="Pad_ClipTop"
  BaseFeature = -> AdditiveLoft001
  Direction = (1,1,1)
  Length = 40
  Length2 = 100
  Midplane = true
  Placement = pos=(0,0,0) rot=(1,0,0;1.5708rad)
  Profile = -> Sketch025
  Type = 0
  expr: Length = <<params>>.ear_front_mid_width * 1.25
FEATURE [Sketcher::SketchObject] Sketch026  label="Sketch_ClipSplit_Bot"
  FullyConstrained = true
  MapMode = 5
  Placement = pos=(0,0,0) rot=(0.57735,0.57735,0.57735;2.0944rad)
  Support = -> [YZ_Plane009]
  expr: Constraints[27] = <<params>>.ear_trim_clip_height - 2 * <<params>>.ear_trim_clip_thick
  expr: Constraints[26] = <<params>>.ear_trim_clip_width
  expr: Constraints[28] = <<params>>.ear_trim_clip_thick + <<params>>.ear_trim_clip_wedge_size
  expr: Constraints[25] = <<params>>.ear_front_mid_height + <<params>>.ear_trim_clip_height + <<params>>.ear_trim_clip_tol / 2
  expr: Constraints[8] = <<params>>.ear_trim_leng
  sketch-geometry (11):
    g0: LineSegment StartX=2.4 StartY=17 StartZ=0 EndX=4 EndY=17 EndZ=0
    g1: LineSegment StartX=4 StartY=17 StartZ=0 EndX=4 EndY=15.8 EndZ=0
    g2: LineSegment StartX=4 StartY=15.8 StartZ=0 EndX=2.4 EndY=15.8 EndZ=0
    g3: LineSegment StartX=2.4 StartY=15.8 StartZ=0 EndX=2.4 EndY=17 EndZ=0
    g4: GeomPoint X=3.2 Y=15.1 Z=0
    g5: LineSegment StartX=2.4 StartY=14.4 StartZ=0 EndX=4 EndY=14.4 EndZ=0
    g6: LineSegment StartX=4 StartY=14.4 StartZ=0 EndX=4 EndY=13.2 EndZ=0
    g7: LineSegment StartX=4 StartY=13.2 StartZ=0 EndX=2.4 EndY=13.2 EndZ=0
    g8: LineSegment StartX=2.4 StartY=13.2 StartZ=0 EndX=2.4 EndY=14.4 EndZ=0
    g9: LineSegment StartX=2.4 StartY=15.8 StartZ=0 EndX=2.4 EndY=14.4 EndZ=0
    g10: LineSegment StartX=4 StartY=15.8 StartZ=0 EndX=4 EndY=14.4 EndZ=0
  constraints (29):
    c: Coincident(g0,g1)
    c: Coincident(g1,g2)
    c: Coincident(g2,g3)
    c: Coincident(g3,g0)
    c: Horizontal(g0)
    c: Horizontal(g2)
    c: Vertical(g1)
    c: Vertical(g3)
    c: DistanceX(g-1,g1) = 4
    c: Coincident(g5,g6)
    c: Coincident(g6,g7)
    c: Coincident(g7,g8)
    c: Coincident(g8,g5)
    c: Horizontal(g5)
    c: Horizontal(g7)
    c: Vertical(g6)
    c: Vertical(g8)
    c: Coincident(g9,g2)
    c: Coincident(g9,g5)
    c: Coincident(g10,g1)
    c: Coincident(g10,g5)
    c: Vertical(g10)
    c: Vertical(g9)
    c: Symmetric(g1,g5,g4)
    c: Equal(g3,g8)
    c: DistanceY(g-1,g4) = 15.1
    c: DistanceX(g7,g6) = 1.6
    c: DistanceY(g5,g1) = 1.4
    c: DistanceY(g1,g0) = 1.2
FEATURE [PartDesign::Pad] Pad010  label="Pad_ClipBot"
  BaseFeature = -> Pad009
  Direction = (1,1,1)
  Length = 40
  Length2 = 100
  Midplane = true
  Placement = pos=(0,0,0) rot=(1,0,0;1.5708rad)
  Profile = -> Sketch026
  Type = 0
  expr: Length = <<params>>.ear_front_mid_width * 1.25
FEATURE [Sketcher::SketchObject] Sketch027  label="Sketch_EarClipFront"
  FullyConstrained = true
  MapMode = 5
  Placement = pos=(0,0,0) rot=(1,0,0;1.5708rad)
  Support = -> [XZ_Plane009]
  expr: Constraints[35] = <<params>>.ear_ellipse_majax
  expr: Constraints[60] = <<params>>.ear_trim_clip_thick
  expr: Constraints[40] = <<params>>.ear_ellipse_majax
  expr: Constraints[32] = <<params>>.ear_front_mid_width
  expr: Constraints[34] = <<params>>.ear_front_tot_height
  expr: Constraints[46] = <<params>>.ear_trim_thick
  expr: Constraints[93] = <<params>>.ear_trim_clip_leng
  expr: Constraints[141] = <<params>>.ear_ellipse_majax
  expr: Constraints[94] = <<params>>.ear_trim_clip_leng
  expr: Constraints[113] = <<params>>.ear_trim_clip_thick + <<params>>.ear_trim_clip_wedge_size
  expr: Constraints[45] = <<params>>.ear_trim_thick
  expr: Constraints[33] = <<params>>.ear_front_base_width
  expr: Constraints[138] = <<params>>.ear_front_mid_height + <<params>>.ear_trim_clip_height + <<params>>.ear_trim_clip_tol / 2
  expr: Constraints[31] = <<params>>.ear_front_mid_height
  expr: Constraints[30] = <<params>>.ear_base_thick + <<params>>.ear_vert_height
  expr: Constraints[140] = <<params>>.ear_trim_clip_height
  sketch-geometry (69):
    g0: LineSegment StartX=-13 StartY=0 StartZ=0 EndX=13 EndY=0 EndZ=0
    g1: LineSegment StartX=-13 StartY=0 StartZ=0 EndX=-13 EndY=3.6 EndZ=0
    g2: LineSegment StartX=13 StartY=0 StartZ=0 EndX=13 EndY=3.6 EndZ=0
    g3: LineSegment StartX=-13 StartY=3.6 StartZ=0 EndX=13 EndY=3.6 EndZ=0
    g4: LineSegment StartX=13 StartY=3.6 StartZ=0 EndX=16 EndY=12 EndZ=0
    g5: LineSegment StartX=-13 StartY=3.6 StartZ=0 EndX=-16 EndY=12 EndZ=0
    g6: ArcOfEllipse CenterX=0 CenterY=4e-16 CenterZ=0 NormalX=0 NormalY=0 NormalZ=1 MajorRadius=40 MinorRadius=16.7726 AngleXU=1.5708 StartAngle=5.01708 EndAngle=7.54929
    g7: LineSegment StartX=0 StartY=40 StartZ=0 EndX=0 EndY=-40 EndZ=0
    g8: LineSegment StartX=-16.7726 StartY=4e-16 StartZ=0 EndX=16.7726 EndY=4e-16 EndZ=0
    g9: GeomPoint X=0 Y=36.3137 Z=0
    g10: GeomPoint X=0 Y=-36.3137 Z=0
    g11: LineSegment StartX=-16 StartY=12 StartZ=0 EndX=16 EndY=12 EndZ=0
    g12: LineSegment StartX=-13 StartY=3.6 StartZ=0 EndX=-13 EndY=12 EndZ=0
    g13: LineSegment StartX=13 StartY=3.6 StartZ=0 EndX=13 EndY=12 EndZ=0
    g14: LineSegment StartX=-16 StartY=12 StartZ=0 EndX=16 EndY=12 EndZ=0
    g15: ArcOfEllipse CenterX=0 CenterY=-1.2 CenterZ=0 NormalX=0 NormalY=0 NormalZ=1 MajorRadius=40 MinorRadius=15.6783 AngleXU=1.5708 StartAngle=5.04869 EndAngle=7.51768
    g16: LineSegment StartX=0 StartY=38.8 StartZ=0 EndX=0 EndY=-41.2 EndZ=0
    g17: LineSegment StartX=-15.6783 StartY=-1.2 StartZ=0 EndX=15.6783 EndY=-1.2 EndZ=0
    g18: GeomPoint X=0 Y=35.5993 Z=0
    g19: GeomPoint X=0 Y=-37.9993 Z=0
    g20: LineSegment StartX=-14.0404 StartY=16.6 StartZ=0 EndX=-12.6404 EndY=16.6 EndZ=0
    g21: LineSegment StartX=-14.1919 StartY=15.8 StartZ=0 EndX=-11.8404 EndY=15.8 EndZ=0
    g22: LineSegment StartX=-12.6404 StartY=16.6 StartZ=0 EndX=-12.6404 EndY=15.8 EndZ=0
    g23: LineSegment StartX=-11.8404 StartY=15.8 StartZ=0 EndX=-11.8404 EndY=16.6 EndZ=0
    g24: LineSegment StartX=-11.8404 StartY=16.6 StartZ=0 EndX=-12.2404 EndY=17 EndZ=0
    g25: LineSegment StartX=-12.6404 StartY=16.6 StartZ=0 EndX=-11.8404 EndY=16.6 EndZ=0
    g26: LineSegment StartX=-12.6404 StartY=16.6 StartZ=0 EndX=-12.2404 EndY=17 EndZ=0
    g27: LineSegment StartX=14.0404 StartY=16.6 StartZ=0 EndX=12.6404 EndY=16.6 EndZ=0
    g28: LineSegment StartX=14.1919 StartY=15.8 StartZ=0 EndX=12.6404 EndY=15.8 EndZ=0
    g29: LineSegment StartX=12.6404 StartY=16.6 StartZ=0 EndX=12.2404 EndY=17 EndZ=0
    g30: LineSegment StartX=12.2404 StartY=17 StartZ=0 EndX=11.8404 EndY=16.6 EndZ=0
    g31: LineSegment StartX=11.8404 StartY=16.6 StartZ=0 EndX=11.8404 EndY=15.8 EndZ=0
    g32: LineSegment StartX=11.8404 StartY=15.8 StartZ=0 EndX=12.6404 EndY=15.8 EndZ=0
    g33: LineSegment StartX=12.6404 StartY=16.6 StartZ=0 EndX=12.6404 EndY=15.8 EndZ=0
    g34: LineSegment StartX=11.8404 StartY=16.6 StartZ=0 EndX=12.6404 EndY=16.6 EndZ=0
    g35: LineSegment StartX=-11.8404 StartY=16.6 StartZ=0 EndX=11.8404 EndY=16.6 EndZ=0
    g36: LineSegment StartX=-11.8404 StartY=15.8 StartZ=0 EndX=11.8404 EndY=15.8 EndZ=0
    g37: LineSegment StartX=-12.2404 StartY=17 StartZ=0 EndX=12.2404 EndY=17 EndZ=0
    g38: LineSegment StartX=-14.8 StartY=12 StartZ=0 EndX=14.8 EndY=12 EndZ=0
    g39: LineSegment StartX=-14.4368 StartY=14.4 StartZ=0 EndX=-14.1919 EndY=15.8 EndZ=0
    g40: LineSegment StartX=-14.0404 StartY=16.6 StartZ=0 EndX=-14.0404 EndY=13.6 EndZ=0
    g41: ArcOfEllipse CenterX=3.9e-15 CenterY=-1.2 CenterZ=0 NormalX=0 NormalY=0 NormalZ=1 MajorRadius=40 MinorRadius=15.6783 AngleXU=1.5708 StartAngle=5.17356 EndAngle=7.39281
    g42: LineSegment StartX=0 StartY=38.8 StartZ=0 EndX=7.9e-15 EndY=-41.2 EndZ=0
    g43: LineSegment StartX=-15.6783 StartY=-1.2 StartZ=0 EndX=15.6783 EndY=-1.2 EndZ=0
    g44: GeomPoint X=3e-16 Y=35.5993 Z=0
    g45: GeomPoint X=7.5e-15 Y=-37.9993 Z=0
    g46: GeomPoint X=-14.0404 Y=15.1 Z=0
    g47: LineSegment StartX=-12.2404 StartY=17 StartZ=0 EndX=-12.2404 EndY=15.8 EndZ=0
    g48: LineSegment StartX=-14.4368 StartY=14.4 StartZ=0 EndX=-13.0368 EndY=14.4 EndZ=0
    g49: LineSegment StartX=-14.5656 StartY=13.6 StartZ=0 EndX=-13.0368 EndY=13.6 EndZ=0
    g50: LineSegment StartX=-13.0368 StartY=14.4 StartZ=0 EndX=-12.2368 EndY=14.4 EndZ=0
    g51: LineSegment StartX=-13.0368 StartY=13.6 StartZ=0 EndX=-12.6368 EndY=13.2 EndZ=0
    g52: LineSegment StartX=-12.6368 StartY=13.2 StartZ=0 EndX=-12.2368 EndY=13.6 EndZ=0
    g53: LineSegment StartX=-12.2368 StartY=13.6 StartZ=0 EndX=-12.2368 EndY=14.4 EndZ=0
    g54: LineSegment StartX=-13.0368 StartY=14.4 StartZ=0 EndX=-13.0368 EndY=13.6 EndZ=0
    g55: LineSegment StartX=-13.0368 StartY=13.6 StartZ=0 EndX=-12.2368 EndY=13.6 EndZ=0
    g56: LineSegment StartX=-12.6368 StartY=13.2 StartZ=0 EndX=-12.6368 EndY=14.4 EndZ=0
    g57: LineSegment StartX=-14.5656 StartY=13.6 StartZ=0 EndX=-14.8 EndY=12 EndZ=0
    g58: LineSegment StartX=14.4368 StartY=14.4 StartZ=0 EndX=13.0368 EndY=14.4 EndZ=0
    g59: LineSegment StartX=13.0368 StartY=14.4 StartZ=0 EndX=12.2368 EndY=14.4 EndZ=0
    g60: LineSegment StartX=12.2368 StartY=14.4 StartZ=0 EndX=12.2368 EndY=13.6 EndZ=0
    g61: LineSegment StartX=12.2368 StartY=13.6 StartZ=0 EndX=12.6368 EndY=13.2 EndZ=0
    g62: LineSegment StartX=12.6368 StartY=13.2 StartZ=0 EndX=13.0368 EndY=13.6 EndZ=0
    g63: LineSegment StartX=13.0368 StartY=13.6 StartZ=0 EndX=14.5656 EndY=13.6 EndZ=0
    g64: LineSegment StartX=13.0368 StartY=13.6 StartZ=0 EndX=13.0368 EndY=14.4 EndZ=0
    g65: LineSegment StartX=12.2368 StartY=13.6 StartZ=0 EndX=13.0368 EndY=13.6 EndZ=0
    g66: LineSegment StartX=-12.2368 StartY=14.4 StartZ=0 EndX=12.2368 EndY=14.4 EndZ=0
    g67: LineSegment StartX=14.1919 StartY=15.8 StartZ=0 EndX=14.4368 EndY=14.4 EndZ=0
    g68: LineSegment StartX=14.5656 StartY=13.6 StartZ=0 EndX=14.8 EndY=12 EndZ=0
  constraints (164):
    c: Horizontal(g0)
    c: Symmetric(g0,g0,g-1)
    c: Coincident(g1,g0)
    c: Vertical(g1)
    c: Coincident(g2,g0)
    c: Vertical(g2)
    c: Coincident(g3,g1)
    c: Coincident(g3,g2)
    c: Horizontal(g3)
    c: Coincident(g4,g2)
    c: Coincident(g5,g1)
    c: InternalAlignment(g7-g10 -> g6) x4
    c: PointOnObject(g6,g-2)
    c: Coincident(g11,g5)
    c: Coincident(g11,g4)
    c: Horizontal(g11)
    c: Coincident(g12,g1)
    c: PointOnObject(g12,g11)
    c: Vertical(g12)
    c: Coincident(g13,g2)
    c: PointOnObject(g13,g11)
    c: Vertical(g13)
    c: PointOnObject(g7,g-2)
    c: Coincident(g14,g6)
    c: Coincident(g14,g6)
    c: Coincident(g6,g5)
    c: Coincident(g6,g4)
    c: DistanceY(g0,g2) = 3.6
    c: DistanceY(g-1,g4) = 12
    c: DistanceX(g5,g4) = 32
    c: DistanceX(g0,g0) = 26
    c: DistanceY(g-1,g7) = 40
    c: DistanceY(g8,g7) = 40
    c: InternalAlignment(g16-g19 -> g15) x4
    c: DistanceY(g17,g16) = 40
    c: Vertical(g16)
    c: PointOnObject(g16,g-2)
    c: PointOnObject(g15,g11)
    c: PointOnObject(g15,g11)
    c: DistanceX(g15,g4) = 1.2
    c: DistanceY(g16,g7) = 1.2
    c: PointOnObject(g20,g15)
    c: Horizontal(g20)
    c: PointOnObject(g21,g15)
    c: Horizontal(g21)
    c: Coincident(g22,g20)
    c: PointOnObject(g22,g21)
    c: Vertical(g22)
    c: Coincident(g23,g21)
    c: Vertical(g23)
    c: Coincident(g24,g23)
    c: Coincident(g25,g20)
    c: Coincident(g25,g23)
    c: Horizontal(g25)
    c: DistanceY(g21,g23) = 0.8
    c: Coincident(g26,g20)
    c: Coincident(g26,g24)
    c: Equal(g24,g26)
    c: Angle(g26,g24) = 1.5708
    c: PointOnObject(g27,g15)
    c: Horizontal(g27)
    c: PointOnObject(g28,g15)
    c: Horizontal(g28)
    c: Coincident(g29,g27)
    c: Coincident(g30,g29)
    c: Coincident(g31,g30)
    c: Vertical(g31)
    c: Coincident(g32,g31)
    c: Coincident(g32,g28)
    c: Coincident(g33,g27)
    c: Coincident(g33,g28)
    c: Coincident(g34,g30)
    c: Coincident(g34,g27)
    c: Horizontal(g34)
    c: Vertical(g33)
    c: Horizontal(g32)
    c: Coincident(g35,g23)
    c: Coincident(g35,g30)
    c: Horizontal(g35)
    c: Coincident(g36,g21)
    c: Coincident(g36,g31)
    c: Horizontal(g36)
    c: Angle(g30,g29) = 1.5708
    c: Coincident(g37,g24)
    c: Coincident(g37,g29)
    c: Horizontal(g37)
    c: Equal(g24,g30)
    c: DistanceX(g20,g20) = 1.4
    c: DistanceX(g27,g27) = 1.4
    c: Coincident(g38,g15)
    c: Coincident(g38,g15)
    c: PointOnObject(g39,g15)
    c: PointOnObject(g49,g15)
    c: Coincident(g39,g21)
    c: Coincident(g40,g20)
    c: Vertical(g40)
    c: InternalAlignment(g42-g45 -> g41) x4
    c: Coincident(g42,g16)
    c: Coincident(g41,g20)
    c: Coincident(g41,g27)
    c: Symmetric(g20,g40,g46)
    c: Coincident(g47,g24)
    c: PointOnObject(g47,g21)
    c: Vertical(g47)
    c: DistanceY(g21,g24) = 1.2
    c: Coincident(g48,g39)
    c: Horizontal(g48)
    c: Horizontal(g49)
    c: PointOnObject(g40,g49)
    c: Coincident(g50,g48)
    c: Horizontal(g50)
    c: Coincident(g51,g49)
    c: Coincident(g52,g51)
    c: Coincident(g53,g52)
    c: Coincident(g53,g50)
    c: Vertical(g53)
    c: Coincident(g54,g48)
    c: Coincident(g54,g49)
    c: Coincident(g55,g49)
    c: Coincident(g55,g52)
    c: Horizontal(g55)
    c: Vertical(g54)
    c: Angle(g52,g51) = 1.5708
    c: Coincident(g56,g51)
    c: PointOnObject(g56,g50)
    c: Vertical(g56)
    c: Equal(g52,g51)
    c: Equal(g52,g24)
    c: Equal(g56,g47)
    c: DistanceY(g-1,g46) = 15.1
    c: Equal(g48,g20)
    c: DistanceY(g52,g23) = 3
    c: DistanceY(g43,g16) = 40
    c: Coincident(g57,g49)
    c: Coincident(g57,g38)
    c: PointOnObject(g58,g15)
    c: Horizontal(g58)
    c: Coincident(g59,g58)
    c: Horizontal(g59)
    c: Coincident(g60,g59)
    c: Vertical(g60)
    c: Coincident(g61,g60)
    c: Coincident(g62,g61)
    c: Coincident(g63,g62)
    c: PointOnObject(g63,g15)
    c: Horizontal(g63)
    c: Coincident(g64,g62)
    c: Coincident(g64,g58)
    c: Vertical(g64)
    c: Coincident(g65,g60)
    c: Coincident(g65,g62)
    c: Horizontal(g65)
    c: Angle(g62,g61) = 1.5708
    c: Equal(g29,g62)
    c: Equal(g61,g62)
    c: Equal(g60,g31)
    c: Equal(g58,g27)
    c: Coincident(g66,g50)
    c: Coincident(g66,g59)
    c: Horizontal(g66)
    c: Coincident(g67,g28)
    c: Coincident(g67,g58)
    c: Coincident(g68,g63)
    c: Coincident(g68,g38)
FEATURE [Sketcher::SketchObject] Sketch028  label="Sketch_EarClipBack"
  FullyConstrained = true
  MapMode = 5
  Placement = pos=(0,4,9e-16) rot=(1,0,0;1.5708rad)
  Support = -> [DatumPlane003]
  expr: Constraints[140] = <<params>>.ear_trim_clip_height
  expr: Constraints[30] = <<params>>.ear_base_thick + <<params>>.ear_vert_height
  expr: Constraints[31] = <<params>>.ear_trim_mid_height
  expr: Constraints[138] = <<params>>.ear_front_mid_height + <<params>>.ear_trim_clip_height + <<params>>.ear_trim_clip_tol / 2
  expr: Constraints[33] = <<params>>.ear_trim_base_width
  expr: Constraints[45] = <<params>>.ear_trim_thick
  expr: Constraints[113] = <<params>>.ear_trim_clip_thick + <<params>>.ear_trim_clip_wedge_size
  expr: Constraints[94] = <<params>>.ear_trim_clip_leng
  expr: Constraints[141] = <<params>>.ear_ellipse_majax
  expr: Constraints[93] = <<params>>.ear_trim_clip_leng
  expr: Constraints[46] = <<params>>.ear_trim_thick
  expr: Constraints[34] = <<params>>.ear_trim_tot_height
  expr: Constraints[32] = <<params>>.ear_trim_mid_width
  expr: Constraints[40] = <<params>>.ear_ellipse_majax
  expr: Constraints[60] = <<params>>.ear_trim_clip_thick
  expr: Constraints[35] = <<params>>.ear_ellipse_majax
  sketch-geometry (69):
    g0: LineSegment StartX=-12.7917 StartY=0 StartZ=0 EndX=12.7917 EndY=0 EndZ=0
    g1: LineSegment StartX=-12.7917 StartY=0 StartZ=0 EndX=-12.7917 EndY=3.6 EndZ=0
    g2: LineSegment StartX=12.7917 StartY=0 StartZ=0 EndX=12.7917 EndY=3.6 EndZ=0
    g3: LineSegment StartX=-12.7917 StartY=3.6 StartZ=0 EndX=12.7917 EndY=3.6 EndZ=0
    g4: LineSegment StartX=12.7917 StartY=3.6 StartZ=0 EndX=15.3333 EndY=11 EndZ=0
    g5: LineSegment StartX=-12.7917 StartY=3.6 StartZ=0 EndX=-15.3333 EndY=11 EndZ=0
    g6: ArcOfEllipse CenterX=0 CenterY=-4.33333 CenterZ=0 NormalX=0 NormalY=0 NormalZ=1 MajorRadius=40 MinorRadius=16.6015 AngleXU=1.5708 StartAngle=5.10579 EndAngle=7.46058
    g7: LineSegment StartX=0 StartY=35.6667 StartZ=0 EndX=0 EndY=-44.3333 EndZ=0
    g8: LineSegment StartX=-16.6015 StartY=-4.33333 StartZ=0 EndX=16.6015 EndY=-4.33333 EndZ=0
    g9: GeomPoint X=0 Y=32.0588 Z=0
    g10: GeomPoint X=0 Y=-40.7255 Z=0
    g11: LineSegment StartX=-15.3333 StartY=11 StartZ=0 EndX=15.3333 EndY=11 EndZ=0
    g12: LineSegment StartX=-12.7917 StartY=3.6 StartZ=0 EndX=-12.7917 EndY=11 EndZ=0
    g13: LineSegment StartX=12.7917 StartY=3.6 StartZ=0 EndX=12.7917 EndY=11 EndZ=0
    g14: LineSegment StartX=-15.3333 StartY=11 StartZ=0 EndX=15.3333 EndY=11 EndZ=0
    g15: ArcOfEllipse CenterX=0 CenterY=-5.53333 CenterZ=0 NormalX=0 NormalY=0 NormalZ=1 MajorRadius=40 MinorRadius=15.5212 AngleXU=1.5708 StartAngle=5.1385 EndAngle=7.42787
    g16: LineSegment StartX=0 StartY=34.4667 StartZ=0 EndX=0 EndY=-45.5333 EndZ=0
    g17: LineSegment StartX=-15.5212 StartY=-5.53333 StartZ=0 EndX=15.5212 EndY=-5.53333 EndZ=0
    g18: GeomPoint X=0 Y=31.3325 Z=0
    g19: GeomPoint X=0 Y=-42.3992 Z=0
    g20: LineSegment StartX=-12.9286 StartY=16.6 StartZ=0 EndX=-11.5286 EndY=16.6 EndZ=0
    g21: LineSegment StartX=-13.1295 StartY=15.8 StartZ=0 EndX=-10.7286 EndY=15.8 EndZ=0
    g22: LineSegment StartX=-11.5286 StartY=16.6 StartZ=0 EndX=-11.5286 EndY=15.8 EndZ=0
    g23: LineSegment StartX=-10.7286 StartY=15.8 StartZ=0 EndX=-10.7286 EndY=16.6 EndZ=0
    g24: LineSegment StartX=-10.7286 StartY=16.6 StartZ=0 EndX=-11.1286 EndY=17 EndZ=0
    g25: LineSegment StartX=-11.5286 StartY=16.6 StartZ=0 EndX=-10.7286 EndY=16.6 EndZ=0
    g26: LineSegment StartX=-11.5286 StartY=16.6 StartZ=0 EndX=-11.1286 EndY=17 EndZ=0
    g27: LineSegment StartX=12.9286 StartY=16.6 StartZ=0 EndX=11.5286 EndY=16.6 EndZ=0
    g28: LineSegment StartX=13.1295 StartY=15.8 StartZ=0 EndX=11.5286 EndY=15.8 EndZ=0
    g29: LineSegment StartX=11.5286 StartY=16.6 StartZ=0 EndX=11.1286 EndY=17 EndZ=0
    g30: LineSegment StartX=11.1286 StartY=17 StartZ=0 EndX=10.7286 EndY=16.6 EndZ=0
    g31: LineSegment StartX=10.7286 StartY=16.6 StartZ=0 EndX=10.7286 EndY=15.8 EndZ=0
    g32: LineSegment StartX=10.7286 StartY=15.8 StartZ=0 EndX=11.5286 EndY=15.8 EndZ=0
    g33: LineSegment StartX=11.5286 StartY=16.6 StartZ=0 EndX=11.5286 EndY=15.8 EndZ=0
    g34: LineSegment StartX=10.7286 StartY=16.6 StartZ=0 EndX=11.5286 EndY=16.6 EndZ=0
    g35: LineSegment StartX=-10.7286 StartY=16.6 StartZ=0 EndX=10.7286 EndY=16.6 EndZ=0
    g36: LineSegment StartX=-10.7286 StartY=15.8 StartZ=0 EndX=10.7286 EndY=15.8 EndZ=0
    g37: LineSegment StartX=-11.1286 StartY=17 StartZ=0 EndX=11.1286 EndY=17 EndZ=0
    g38: LineSegment StartX=-14.1333 StartY=11 StartZ=0 EndX=14.1333 EndY=11 EndZ=0
    g39: LineSegment StartX=-13.4567 StartY=14.4 StartZ=0 EndX=-13.1295 EndY=15.8 EndZ=0
    g40: LineSegment StartX=-12.9286 StartY=16.6 StartZ=0 EndX=-12.9286 EndY=13.6 EndZ=0
    g41: ArcOfEllipse CenterX=-1.46e-14 CenterY=-5.53333 CenterZ=0 NormalX=0 NormalY=0 NormalZ=1 MajorRadius=40 MinorRadius=15.5212 AngleXU=1.5708 StartAngle=5.29875 EndAngle=7.26762
    g42: LineSegment StartX=0 StartY=34.4667 StartZ=0 EndX=-2.92e-14 EndY=-45.5333 EndZ=0
    g43: LineSegment StartX=-15.5212 StartY=-5.53333 StartZ=0 EndX=15.5212 EndY=-5.53333 EndZ=0
    g44: GeomPoint X=-1.1e-15 Y=31.3325 Z=0
    g45: GeomPoint X=-2.8e-14 Y=-42.3992 Z=0
    g46: GeomPoint X=-12.9286 Y=15.1 Z=0
    g47: LineSegment StartX=-11.1286 StartY=17 StartZ=0 EndX=-11.1286 EndY=15.8 EndZ=0
    g48: LineSegment StartX=-13.4567 StartY=14.4 StartZ=0 EndX=-12.0567 EndY=14.4 EndZ=0
    g49: LineSegment StartX=-13.6304 StartY=13.6 StartZ=0 EndX=-12.0567 EndY=13.6 EndZ=0
    g50: LineSegment StartX=-12.0567 StartY=14.4 StartZ=0 EndX=-11.2567 EndY=14.4 EndZ=0
    g51: LineSegment StartX=-12.0567 StartY=13.6 StartZ=0 EndX=-11.6567 EndY=13.2 EndZ=0
    g52: LineSegment StartX=-11.6567 StartY=13.2 StartZ=0 EndX=-11.2567 EndY=13.6 EndZ=0
    g53: LineSegment StartX=-11.2567 StartY=13.6 StartZ=0 EndX=-11.2567 EndY=14.4 EndZ=0
    g54: LineSegment StartX=-12.0567 StartY=14.4 StartZ=0 EndX=-12.0567 EndY=13.6 EndZ=0
    g55: LineSegment StartX=-12.0567 StartY=13.6 StartZ=0 EndX=-11.2567 EndY=13.6 EndZ=0
    g56: LineSegment StartX=-11.6567 StartY=13.2 StartZ=0 EndX=-11.6567 EndY=14.4 EndZ=0
    g57: LineSegment StartX=-13.6304 StartY=13.6 StartZ=0 EndX=-14.1333 EndY=11 EndZ=0
    g58: LineSegment StartX=13.4567 StartY=14.4 StartZ=0 EndX=12.0567 EndY=14.4 EndZ=0
    g59: LineSegment StartX=12.0567 StartY=14.4 StartZ=0 EndX=11.2567 EndY=14.4 EndZ=0
    g60: LineSegment StartX=11.2567 StartY=14.4 StartZ=0 EndX=11.2567 EndY=13.6 EndZ=0
    g61: LineSegment StartX=11.2567 StartY=13.6 StartZ=0 EndX=11.6567 EndY=13.2 EndZ=0
    g62: LineSegment StartX=11.6567 StartY=13.2 StartZ=0 EndX=12.0567 EndY=13.6 EndZ=0
    g63: LineSegment StartX=12.0567 StartY=13.6 StartZ=0 EndX=13.6304 EndY=13.6 EndZ=0
    g64: LineSegment StartX=12.0567 StartY=13.6 StartZ=0 EndX=12.0567 EndY=14.4 EndZ=0
    g65: LineSegment StartX=11.2567 StartY=13.6 StartZ=0 EndX=12.0567 EndY=13.6 EndZ=0
    g66: LineSegment StartX=-11.2567 StartY=14.4 StartZ=0 EndX=11.2567 EndY=14.4 EndZ=0
    g67: LineSegment StartX=13.1295 StartY=15.8 StartZ=0 EndX=13.4567 EndY=14.4 EndZ=0
    g68: LineSegment StartX=13.6304 StartY=13.6 StartZ=0 EndX=14.1333 EndY=11 EndZ=0
  constraints (164):
    c: Horizontal(g0)
    c: Symmetric(g0,g0,g-1)
    c: Coincident(g1,g0)
    c: Vertical(g1)
    c: Coincident(g2,g0)
    c: Vertical(g2)
    c: Coincident(g3,g1)
    c: Coincident(g3,g2)
    c: Horizontal(g3)
    c: Coincident(g4,g2)
    c: Coincident(g5,g1)
    c: InternalAlignment(g7-g10 -> g6) x4
    c: PointOnObject(g6,g-2)
    c: Coincident(g11,g5)
    c: Coincident(g11,g4)
    c: Horizontal(g11)
    c: Coincident(g12,g1)
    c: PointOnObject(g12,g11)
    c: Vertical(g12)
    c: Coincident(g13,g2)
    c: PointOnObject(g13,g11)
    c: Vertical(g13)
    c: PointOnObject(g7,g-2)
    c: Coincident(g14,g6)
    c: Coincident(g14,g6)
    c: Coincident(g6,g5)
    c: Coincident(g6,g4)
    c: DistanceY(g0,g2) = 3.6
    c: DistanceY(g-1,g4) = 11
    c: DistanceX(g5,g4) = 30.6667
    c: DistanceX(g0,g0) = 25.5833
    c: DistanceY(g-1,g7) = 35.6667
    c: DistanceY(g8,g7) = 40
    c: InternalAlignment(g16-g19 -> g15) x4
    c: DistanceY(g17,g16) = 40
    c: Vertical(g16)
    c: PointOnObject(g16,g-2)
    c: PointOnObject(g15,g11)
    c: PointOnObject(g15,g11)
    c: DistanceX(g15,g4) = 1.2
    c: DistanceY(g16,g7) = 1.2
    c: PointOnObject(g20,g15)
    c: Horizontal(g20)
    c: PointOnObject(g21,g15)
    c: Horizontal(g21)
    c: Coincident(g22,g20)
    c: PointOnObject(g22,g21)
    c: Vertical(g22)
    c: Coincident(g23,g21)
    c: Vertical(g23)
    c: Coincident(g24,g23)
    c: Coincident(g25,g20)
    c: Coincident(g25,g23)
    c: Horizontal(g25)
    c: DistanceY(g21,g23) = 0.8
    c: Coincident(g26,g20)
    c: Coincident(g26,g24)
    c: Equal(g24,g26)
    c: Angle(g26,g24) = 1.5708
    c: PointOnObject(g27,g15)
    c: Horizontal(g27)
    c: PointOnObject(g28,g15)
    c: Horizontal(g28)
    c: Coincident(g29,g27)
    c: Coincident(g30,g29)
    c: Coincident(g31,g30)
    c: Vertical(g31)
    c: Coincident(g32,g31)
    c: Coincident(g32,g28)
    c: Coincident(g33,g27)
    c: Coincident(g33,g28)
    c: Coincident(g34,g30)
    c: Coincident(g34,g27)
    c: Horizontal(g34)
    c: Vertical(g33)
    c: Horizontal(g32)
    c: Coincident(g35,g23)
    c: Coincident(g35,g30)
    c: Horizontal(g35)
    c: Coincident(g36,g21)
    c: Coincident(g36,g31)
    c: Horizontal(g36)
    c: Angle(g30,g29) = 1.5708
    c: Coincident(g37,g24)
    c: Coincident(g37,g29)
    c: Horizontal(g37)
    c: Equal(g24,g30)
    c: DistanceX(g20,g20) = 1.4
    c: DistanceX(g27,g27) = 1.4
    c: Coincident(g38,g15)
    c: Coincident(g38,g15)
    c: PointOnObject(g39,g15)
    c: PointOnObject(g49,g15)
    c: Coincident(g39,g21)
    c: Coincident(g40,g20)
    c: Vertical(g40)
    c: InternalAlignment(g42-g45 -> g41) x4
    c: Coincident(g42,g16)
    c: Coincident(g41,g20)
    c: Coincident(g41,g27)
    c: Symmetric(g20,g40,g46)
    c: Coincident(g47,g24)
    c: PointOnObject(g47,g21)
    c: Vertical(g47)
    c: DistanceY(g21,g24) = 1.2
    c: Coincident(g48,g39)
    c: Horizontal(g48)
    c: Horizontal(g49)
    c: PointOnObject(g40,g49)
    c: Coincident(g50,g48)
    c: Horizontal(g50)
    c: Coincident(g51,g49)
    c: Coincident(g52,g51)
    c: Coincident(g53,g52)
    c: Coincident(g53,g50)
    c: Vertical(g53)
    c: Coincident(g54,g48)
    c: Coincident(g54,g49)
    c: Coincident(g55,g49)
    c: Coincident(g55,g52)
    c: Horizontal(g55)
    c: Vertical(g54)
    c: Angle(g52,g51) = 1.5708
    c: Coincident(g56,g51)
    c: PointOnObject(g56,g50)
    c: Vertical(g56)
    c: Equal(g52,g51)
    c: Equal(g52,g24)
    c: Equal(g56,g47)
    c: DistanceY(g-1,g46) = 15.1
    c: Equal(g48,g20)
    c: DistanceY(g52,g23) = 3
    c: DistanceY(g43,g16) = 40
    c: Coincident(g57,g49)
    c: Coincident(g57,g38)
    c: PointOnObject(g58,g15)
    c: Horizontal(g58)
    c: Coincident(g59,g58)
    c: Horizontal(g59)
    c: Coincident(g60,g59)
    c: Vertical(g60)
    c: Coincident(g61,g60)
    c: Coincident(g62,g61)
    c: Coincident(g63,g62)
    c: PointOnObject(g63,g15)
    c: Horizontal(g63)
    c: Coincident(g64,g62)
    c: Coincident(g64,g58)
    c: Vertical(g64)
    c: Coincident(g65,g60)
    c: Coincident(g65,g62)
    c: Horizontal(g65)
    c: Angle(g62,g61) = 1.5708
    c: Equal(g29,g62)
    c: Equal(g61,g62)
    c: Equal(g60,g31)
    c: Equal(g58,g27)
    c: Coincident(g66,g50)
    c: Coincident(g66,g59)
    c: Horizontal(g66)
    c: Coincident(g67,g28)
    c: Coincident(g67,g58)
    c: Coincident(g68,g63)
    c: Coincident(g68,g38)
FEATURE [PartDesign::SubtractiveLoft] SubtractiveLoft002  label="SubtractiveLoft_TrimClips"
  BaseFeature = -> Pad010
  Closed = false
  Placement = pos=(0,0,0) rot=(1,0,0;1.5708rad)
  Profile = -> Sketch027
  Ruled = false
  Sections = -> [Sketch028]
FEATURE [Sketcher::SketchObject] Sketch029  label="Sketch_EarClipTrimFr001"
  FullyConstrained = true
  MapMode = 5
  Placement = pos=(0,0,0) rot=(1,0,0;1.5708rad)
  Support = -> [XZ_Plane009]
  expr: Constraints[55] = <<params>>.ear_ellipse_majax
  expr: Constraints[70] = <<params>>.ear_front_tot_height / 2
  expr: Constraints[46] = <<params>>.ear_trim_thick
  expr: Constraints[40] = <<params>>.ear_ellipse_majax
  expr: Constraints[35] = <<params>>.ear_ellipse_majax
  expr: Constraints[34] = <<params>>.ear_front_tot_height
  expr: Constraints[45] = <<params>>.ear_trim_thick
  expr: Constraints[33] = <<params>>.ear_front_base_width
  expr: Constraints[32] = <<params>>.ear_front_mid_width
  expr: Constraints[31] = <<params>>.ear_front_mid_height
  expr: Constraints[30] = <<params>>.ear_base_thick + <<params>>.ear_vert_height
  expr: Constraints[72] = <<params>>.ear_front_mid_width / 2
  sketch-geometry (32):
    g0: LineSegment StartX=-13 StartY=0 StartZ=0 EndX=13 EndY=0 EndZ=0
    g1: LineSegment StartX=-13 StartY=0 StartZ=0 EndX=-13 EndY=3.6 EndZ=0
    g2: LineSegment StartX=13 StartY=0 StartZ=0 EndX=13 EndY=3.6 EndZ=0
    g3: LineSegment StartX=-13 StartY=3.6 StartZ=0 EndX=13 EndY=3.6 EndZ=0
    g4: LineSegment StartX=13 StartY=3.6 StartZ=0 EndX=16 EndY=12 EndZ=0
    g5: LineSegment StartX=-13 StartY=3.6 StartZ=0 EndX=-16 EndY=12 EndZ=0
    g6: ArcOfEllipse CenterX=0 CenterY=-2e-16 CenterZ=0 NormalX=0 NormalY=0 NormalZ=1 MajorRadius=40 MinorRadius=16.7726 AngleXU=1.5708 StartAngle=5.01708 EndAngle=7.54929
    g7: LineSegment StartX=0 StartY=40 StartZ=0 EndX=0 EndY=-40 EndZ=0
    g8: LineSegment StartX=-16.7726 StartY=-2e-16 StartZ=0 EndX=16.7726 EndY=-2e-16 EndZ=0
    g9: GeomPoint X=0 Y=36.3137 Z=0
    g10: GeomPoint X=0 Y=-36.3137 Z=0
    g11: LineSegment StartX=-16 StartY=12 StartZ=0 EndX=16 EndY=12 EndZ=0
    g12: LineSegment StartX=-13 StartY=3.6 StartZ=0 EndX=-13 EndY=12 EndZ=0
    g13: LineSegment StartX=13 StartY=3.6 StartZ=0 EndX=13 EndY=12 EndZ=0
    g14: LineSegment StartX=-16 StartY=12 StartZ=0 EndX=16 EndY=12 EndZ=0
    g15: ArcOfEllipse CenterX=0 CenterY=-1.2 CenterZ=0 NormalX=0 NormalY=0 NormalZ=1 MajorRadius=40 MinorRadius=15.6783 AngleXU=1.5708 StartAngle=5.04869 EndAngle=7.51768
    g16: LineSegment StartX=0 StartY=38.8 StartZ=0 EndX=0 EndY=-41.2 EndZ=0
    g17: LineSegment StartX=-15.6783 StartY=-1.2 StartZ=0 EndX=15.6783 EndY=-1.2 EndZ=0
    g18: GeomPoint X=0 Y=35.5993 Z=0
    g19: GeomPoint X=0 Y=-37.9993 Z=0
    g20: LineSegment StartX=-14.8 StartY=12 StartZ=0 EndX=-16 EndY=12 EndZ=0
    g21: LineSegment StartX=14.8 StartY=12 StartZ=0 EndX=16 EndY=12 EndZ=0
    g22: ArcOfEllipse CenterX=8e-16 CenterY=-6e-16 CenterZ=0 NormalX=0 NormalY=0 NormalZ=1 MajorRadius=40 MinorRadius=16.7726 AngleXU=1.5708 StartAngle=5.01708 EndAngle=7.54929
    g23: LineSegment StartX=0 StartY=40 StartZ=0 EndX=1.5e-15 EndY=-40 EndZ=0
    g24: LineSegment StartX=-16.7726 StartY=-9e-16 StartZ=0 EndX=16.7726 EndY=-3e-16 EndZ=0
    g25: GeomPoint X=1e-16 Y=36.3137 Z=0
    g26: GeomPoint X=1.4e-15 Y=-36.3137 Z=0
    g27: LineSegment StartX=16 StartY=12 StartZ=0 EndX=32 EndY=12 EndZ=0
    g28: LineSegment StartX=-16 StartY=12 StartZ=0 EndX=-32 EndY=12 EndZ=0
    g29: LineSegment StartX=-32 StartY=12 StartZ=0 EndX=-32 EndY=60 EndZ=0
    g30: LineSegment StartX=-32 StartY=60 StartZ=0 EndX=32 EndY=60 EndZ=0
    g31: LineSegment StartX=32 StartY=60 StartZ=0 EndX=32 EndY=12 EndZ=0
  constraints (64):
    c: Horizontal(g0)
    c: Symmetric(g0,g0,g-1)
    c: Coincident(g1,g0)
    c: Vertical(g1)
    c: Coincident(g2,g0)
    c: Vertical(g2)
    c: Coincident(g3,g1)
    c: Coincident(g3,g2)
    c: Horizontal(g3)
    c: Coincident(g4,g2)
    c: Coincident(g5,g1)
    c: InternalAlignment(g7-g10 -> g6) x4
    c: PointOnObject(g6,g-2)
    c: Coincident(g11,g5)
    c: Coincident(g11,g4)
    c: Horizontal(g11)
    c: Coincident(g12,g1)
    c: PointOnObject(g12,g11)
    c: Vertical(g12)
    c: Coincident(g13,g2)
    c: PointOnObject(g13,g11)
    c: Vertical(g13)
    c: PointOnObject(g7,g-2)
    c: Coincident(g14,g6)
    c: Coincident(g14,g6)
    c: Coincident(g6,g5)
    c: Coincident(g6,g4)
    c: DistanceY(g0,g2) = 3.6
    c: DistanceY(g-1,g4) = 12
    c: DistanceX(g5,g4) = 32
    c: DistanceX(g0,g0) = 26
    c: DistanceY(g-1,g7) = 40
    c: DistanceY(g8,g7) = 40
    c: InternalAlignment(g16-g19 -> g15) x4
    c: DistanceY(g17,g16) = 40
    c: Vertical(g16)
    c: PointOnObject(g16,g-2)
    c: PointOnObject(g15,g11)
    c: PointOnObject(g15,g11)
    c: DistanceX(g15,g4) = 1.2
    c: DistanceY(g16,g7) = 1.2
    c: Coincident(g20,g15)
    c: Coincident(g20,g5)
    c: Coincident(g21,g15)
    c: Coincident(g21,g4)
    c: InternalAlignment(g23-g26 -> g22) x4
    c: DistanceY(g22,g23) = 40
    c: Coincident(g22,g20)
    c: Coincident(g22,g21)
    c: Coincident(g23,g7)
    c: Coincident(g27,g22)
    c: Horizontal(g27)
    c: Coincident(g28,g22)
    c: Horizontal(g28)
    c: Coincident(g29,g28)
    c: Vertical(g29)
    c: Coincident(g30,g29)
    c: Horizontal(g30)
    c: Coincident(g31,g30)
    c: Coincident(g31,g27)
    c: Vertical(g31)
    c: DistanceY(g7,g30) = 20
    c: Equal(g27,g28)
    c: DistanceX(g22,g27) = 16
FEATURE [Sketcher::SketchObject] Sketch030  label="Sketch_EarClipTrimBk001"
  FullyConstrained = true
  MapMode = 5
  Placement = pos=(0,4,9e-16) rot=(1,0,0;1.5708rad)
  Support = -> [DatumPlane003]
  expr: Constraints[30] = <<params>>.ear_base_thick + <<params>>.ear_vert_height
  expr: Constraints[31] = <<params>>.ear_trim_mid_height
  expr: Constraints[32] = <<params>>.ear_trim_mid_width
  expr: Constraints[33] = <<params>>.ear_trim_base_width
  expr: Constraints[45] = <<params>>.ear_trim_thick
  expr: Constraints[71] = <<params>>.ear_front_mid_width / 2
  expr: Constraints[34] = <<params>>.ear_trim_tot_height
  expr: Constraints[35] = <<params>>.ear_ellipse_majax
  expr: Constraints[40] = <<params>>.ear_ellipse_majax
  expr: Constraints[46] = <<params>>.ear_trim_thick
  expr: Constraints[55] = <<params>>.ear_ellipse_majax
  expr: Constraints[72] = <<params>>.ear_front_tot_height / 2
  sketch-geometry (32):
    g0: LineSegment StartX=-12.7917 StartY=0 StartZ=0 EndX=12.7917 EndY=0 EndZ=0
    g1: LineSegment StartX=-12.7917 StartY=0 StartZ=0 EndX=-12.7917 EndY=3.6 EndZ=0
    g2: LineSegment StartX=12.7917 StartY=0 StartZ=0 EndX=12.7917 EndY=3.6 EndZ=0
    g3: LineSegment StartX=-12.7917 StartY=3.6 StartZ=0 EndX=12.7917 EndY=3.6 EndZ=0
    g4: LineSegment StartX=12.7917 StartY=3.6 StartZ=0 EndX=15.3333 EndY=11 EndZ=0
    g5: LineSegment StartX=-12.7917 StartY=3.6 StartZ=0 EndX=-15.3333 EndY=11 EndZ=0
    g6: ArcOfEllipse CenterX=0 CenterY=-4.33333 CenterZ=0 NormalX=0 NormalY=0 NormalZ=1 MajorRadius=40 MinorRadius=16.6015 AngleXU=1.5708 StartAngle=5.10579 EndAngle=7.46058
    g7: LineSegment StartX=0 StartY=35.6667 StartZ=0 EndX=0 EndY=-44.3333 EndZ=0
    g8: LineSegment StartX=-16.6015 StartY=-4.33333 StartZ=0 EndX=16.6015 EndY=-4.33333 EndZ=0
    g9: GeomPoint X=0 Y=32.0588 Z=0
    g10: GeomPoint X=0 Y=-40.7255 Z=0
    g11: LineSegment StartX=-15.3333 StartY=11 StartZ=0 EndX=15.3333 EndY=11 EndZ=0
    g12: LineSegment StartX=-12.7917 StartY=3.6 StartZ=0 EndX=-12.7917 EndY=11 EndZ=0
    g13: LineSegment StartX=12.7917 StartY=3.6 StartZ=0 EndX=12.7917 EndY=11 EndZ=0
    g14: LineSegment StartX=-15.3333 StartY=11 StartZ=0 EndX=15.3333 EndY=11 EndZ=0
    g15: ArcOfEllipse CenterX=0 CenterY=-5.53333 CenterZ=0 NormalX=0 NormalY=0 NormalZ=1 MajorRadius=40 MinorRadius=15.5212 AngleXU=1.5708 StartAngle=5.1385 EndAngle=7.42787
    g16: LineSegment StartX=0 StartY=34.4667 StartZ=0 EndX=0 EndY=-45.5333 EndZ=0
    g17: LineSegment StartX=-15.5212 StartY=-5.53333 StartZ=0 EndX=15.5212 EndY=-5.53333 EndZ=0
    g18: GeomPoint X=0 Y=31.3325 Z=0
    g19: GeomPoint X=0 Y=-42.3992 Z=0
    g20: LineSegment StartX=-14.1333 StartY=11 StartZ=0 EndX=-15.3333 EndY=11 EndZ=0
    g21: LineSegment StartX=14.1333 StartY=11 StartZ=0 EndX=15.3333 EndY=11 EndZ=0
    g22: ArcOfEllipse CenterX=-1.7e-15 CenterY=-4.33333 CenterZ=0 NormalX=0 NormalY=0 NormalZ=1 MajorRadius=40 MinorRadius=16.6015 AngleXU=1.5708 StartAngle=5.10579 EndAngle=7.46058
    g23: LineSegment StartX=0 StartY=35.6667 StartZ=0 EndX=-3.4e-15 EndY=-44.3333 EndZ=0
    g24: LineSegment StartX=-16.6015 StartY=-4.33333 StartZ=0 EndX=16.6015 EndY=-4.33333 EndZ=0
    g25: GeomPoint X=-2e-16 Y=32.0588 Z=0
    g26: GeomPoint X=-3.3e-15 Y=-40.7255 Z=0
    g27: LineSegment StartX=15.3333 StartY=11 StartZ=0 EndX=31.3333 EndY=11 EndZ=0
    g28: LineSegment StartX=31.3333 StartY=11 StartZ=0 EndX=31.3333 EndY=55.6667 EndZ=0
    g29: LineSegment StartX=31.3333 StartY=55.6667 StartZ=0 EndX=-31.3333 EndY=55.6667 EndZ=0
    g30: LineSegment StartX=-31.3333 StartY=55.6667 StartZ=0 EndX=-31.3333 EndY=11 EndZ=0
    g31: LineSegment StartX=-31.3333 StartY=11 StartZ=0 EndX=-15.3333 EndY=11 EndZ=0
  constraints (64):
    c: Horizontal(g0)
    c: Symmetric(g0,g0,g-1)
    c: Coincident(g1,g0)
    c: Vertical(g1)
    c: Coincident(g2,g0)
    c: Vertical(g2)
    c: Coincident(g3,g1)
    c: Coincident(g3,g2)
    c: Horizontal(g3)
    c: Coincident(g4,g2)
    c: Coincident(g5,g1)
    c: InternalAlignment(g7-g10 -> g6) x4
    c: PointOnObject(g6,g-2)
    c: Coincident(g11,g5)
    c: Coincident(g11,g4)
    c: Horizontal(g11)
    c: Coincident(g12,g1)
    c: PointOnObject(g12,g11)
    c: Vertical(g12)
    c: Coincident(g13,g2)
    c: PointOnObject(g13,g11)
    c: Vertical(g13)
    c: PointOnObject(g7,g-2)
    c: Coincident(g14,g6)
    c: Coincident(g14,g6)
    c: Coincident(g6,g5)
    c: Coincident(g6,g4)
    c: DistanceY(g0,g2) = 3.6
    c: DistanceY(g-1,g4) = 11
    c: DistanceX(g5,g4) = 30.6667
    c: DistanceX(g0,g0) = 25.5833
    c: DistanceY(g-1,g7) = 35.6667
    c: DistanceY(g8,g7) = 40
    c: InternalAlignment(g16-g19 -> g15) x4
    c: DistanceY(g17,g16) = 40
    c: Vertical(g16)
    c: PointOnObject(g16,g-2)
    c: PointOnObject(g15,g11)
    c: PointOnObject(g15,g11)
    c: DistanceX(g15,g4) = 1.2
    c: DistanceY(g16,g7) = 1.2
    c: Coincident(g20,g15)
    c: Coincident(g20,g5)
    c: Coincident(g21,g15)
    c: Coincident(g21,g4)
    c: InternalAlignment(g23-g26 -> g22) x4
    c: DistanceY(g22,g23) = 40
    c: Coincident(g22,g20)
    c: Coincident(g22,g21)
    c: Coincident(g23,g7)
    c: Coincident(g27,g22)
    c: Horizontal(g27)
    c: Coincident(g28,g27)
    c: Vertical(g28)
    c: Coincident(g29,g28)
    c: Horizontal(g29)
    c: Coincident(g30,g29)
    c: Vertical(g30)
    c: Coincident(g31,g30)
    c: Coincident(g31,g22)
    c: Horizontal(g31)
    c: Equal(g27,g31)
    c: DistanceX(g22,g27) = 16
    c: DistanceY(g7,g28) = 20
FEATURE [PartDesign::SubtractiveLoft] SubtractiveLoft003
  BaseFeature = -> SubtractiveLoft002
  Closed = false
  Placement = pos=(0,0,0) rot=(1,0,0;1.5708rad)
  Profile = -> Sketch029
  Ruled = false
  Sections = -> [Sketch030]
FEATURE [PartDesign::Body] Body008  label="EarTrim"
  Group = -> [Sketch020,DatumPlane003,Sketch021,AdditiveLoft001,Sketch025,Pad009,Sketch026,Pad010,Sketch027,Sketch028,SubtractiveLoft002,Sketch029,Sketch030,SubtractiveLoft003]
  Origin = -> Origin010
  Tip = -> SubtractiveLoft003
FEATURE [App::Part] Part  label="Part_EarMt"
  Group = -> [Body,Body008]
  Origin = -> Origin
FEATURE [Mesh::Feature] Mesh  label="EarMt (Meshed)"
FEATURE [Mesh::Feature] Mesh001  label="EarTrim (Meshed)"
